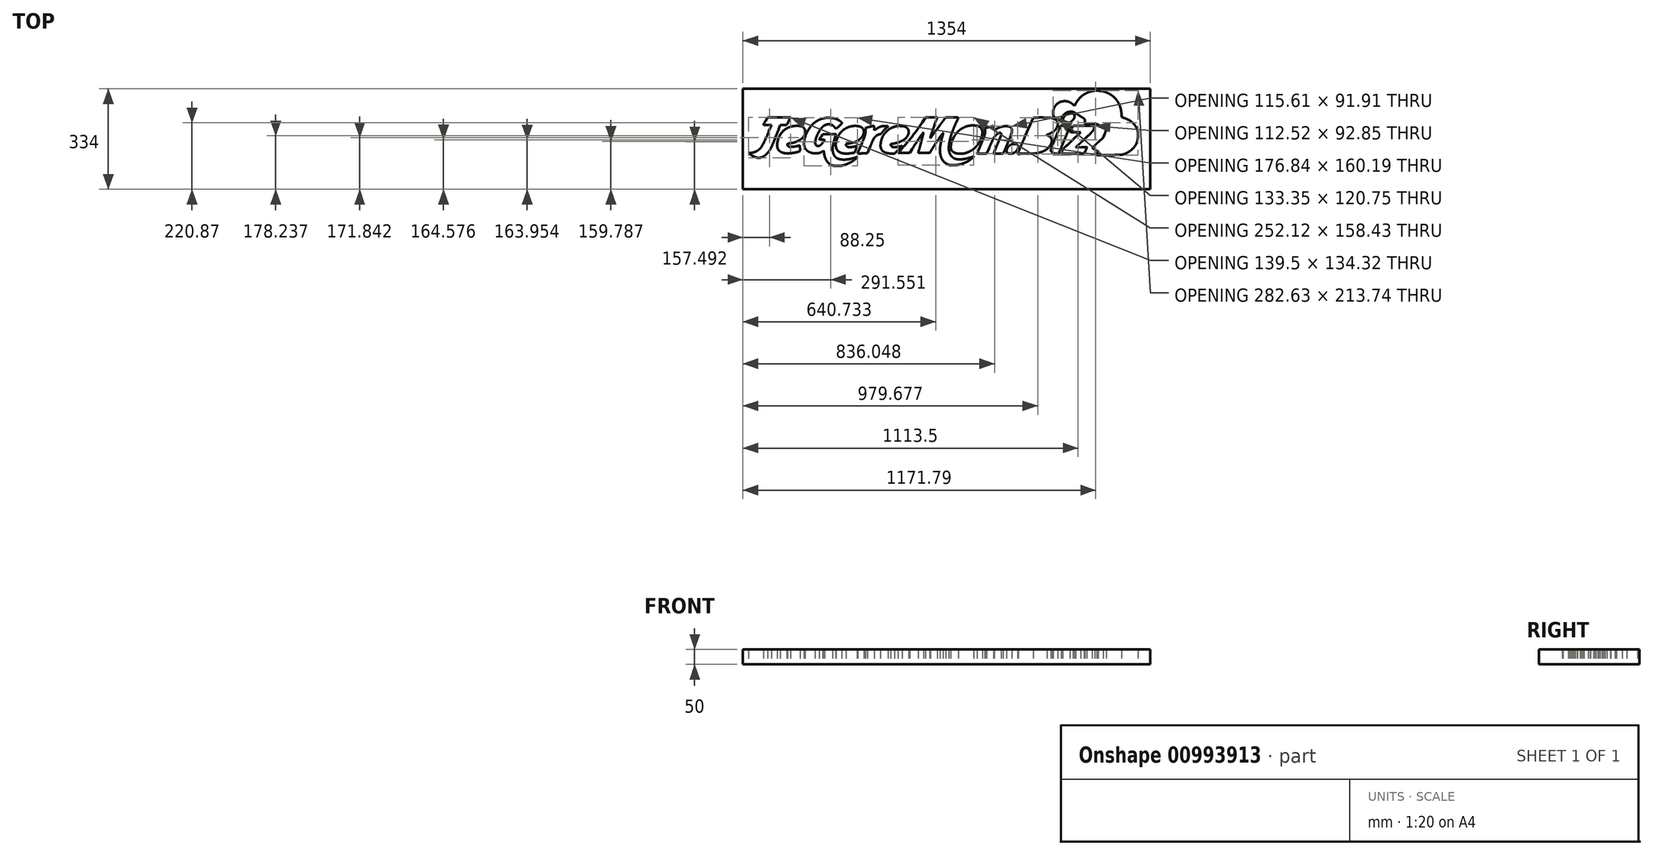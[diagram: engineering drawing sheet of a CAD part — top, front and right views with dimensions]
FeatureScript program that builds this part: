
annotation { "Feature Type Name" : "Feature", "Feature Type Description" : "" }
export const myFeature = defineFeature(function(context is Context, id is Id, definition is map)
    precondition{}
    {
        {
            var Q0;
            Q0=qCreatedBy(makeId("Top.planeOp"),FACE);
            var sketch = newSketch(context, id + "F0", { "sketchPlane" : qUnion([Q0])});
            skLineSegment(sketch, "E0", {"start": v(-677, 0) * mm, "end": v(-677, -167) * mm});
            skLineSegment(sketch, "E1", {"start": v(-677, -167) * mm, "end": v(0, -167) * mm});
            skLineSegment(sketch, "E2", {"start": v(0, -167) * mm, "end": v(677, -167) * mm});
            skLineSegment(sketch, "E3", {"start": v(677, -167) * mm, "end": v(677, 0) * mm});
            skLineSegment(sketch, "E4", {"start": v(677, 0) * mm, "end": v(677, 167) * mm});
            skLineSegment(sketch, "E5", {"start": v(677, 167) * mm, "end": v(0, 167) * mm});
            skLineSegment(sketch, "E6", {"start": v(0, 167) * mm, "end": v(-677, 167) * mm});
            skLineSegment(sketch, "E7", {"start": v(-677, 167) * mm, "end": v(-677, 0) * mm});
            skArc(sketch, "E8", {"start": v(522.85, 158.05) * mm, "mid": v(532, 154.5) * mm, "end": v(540.8, 150.2) * mm});
            skArc(sketch, "E9", {"start": v(540.8, 150.2) * mm, "mid": v(548.3, 145.56) * mm, "end": v(555.24, 140.1) * mm});
            skArc(sketch, "E10", {"start": v(555.24, 140.1) * mm, "mid": v(561.22, 134.1) * mm, "end": v(566.43, 127.43) * mm});
            skArc(sketch, "E11", {"start": v(566.43, 127.43) * mm, "mid": v(571, 119.94) * mm, "end": v(574.75, 112) * mm});
            skArc(sketch, "E12", {"start": v(574.75, 112) * mm, "mid": v(576.07, 108.55) * mm, "end": v(577.26, 105.05) * mm});
            skArc(sketch, "E13", {"start": v(577.26, 105.05) * mm, "mid": v(578.21, 101.76) * mm, "end": v(579, 98.43) * mm});
            skArc(sketch, "E14", {"start": v(579, 98.43) * mm, "mid": v(579.66, 94.87) * mm, "end": v(580.16, 91.29) * mm});
            skArc(sketch, "E15", {"start": v(580.16, 91.29) * mm, "mid": v(580.6, 87) * mm, "end": v(580.91, 82.7) * mm});
            skLineSegment(sketch, "E16", {"start": v(580.91, 82.7) * mm, "end": v(581.5, 72.9) * mm});
            skLineSegment(sketch, "E17", {"start": v(581.5, 72.9) * mm, "end": v(590.5, 69.9) * mm});
            skArc(sketch, "E18", {"start": v(590.5, 69.9) * mm, "mid": v(598.28, 66.89) * mm, "end": v(605.75, 63.2) * mm});
            skArc(sketch, "E19", {"start": v(605.75, 63.2) * mm, "mid": v(612.16, 59.14) * mm, "end": v(618.04, 54.34) * mm});
            skArc(sketch, "E20", {"start": v(618.04, 54.34) * mm, "mid": v(623.04, 49.1) * mm, "end": v(627.33, 43.28) * mm});
            skArc(sketch, "E21", {"start": v(627.33, 43.28) * mm, "mid": v(630.92, 36.86) * mm, "end": v(633.71, 30.06) * mm});
            skArc(sketch, "E22", {"start": v(633.71, 30.06) * mm, "mid": v(635.18, 24.64) * mm, "end": v(635.92, 19.07) * mm});
            skArc(sketch, "E23", {"start": v(635.92, 19.07) * mm, "mid": v(636.1, 12.6) * mm, "end": v(635.72, 6.13) * mm});
            skArc(sketch, "E24", {"start": v(635.72, 6.13) * mm, "mid": v(634.77, -0.46) * mm, "end": v(633.28, -6.94) * mm});
            skArc(sketch, "E25", {"start": v(633.28, -6.94) * mm, "mid": v(631.36, -12.75) * mm, "end": v(628.82, -18.31) * mm});
            skArc(sketch, "E26", {"start": v(628.82, -18.31) * mm, "mid": v(626.67, -21.97) * mm, "end": v(624.15, -25.39) * mm});
            skArc(sketch, "E27", {"start": v(624.15, -25.39) * mm, "mid": v(620.76, -29.27) * mm, "end": v(617.16, -32.96) * mm});
            skArc(sketch, "E28", {"start": v(617.16, -32.96) * mm, "mid": v(613.27, -36.5) * mm, "end": v(609.2, -39.8) * mm});
            skArc(sketch, "E29", {"start": v(609.2, -39.8) * mm, "mid": v(605.45, -42.4) * mm, "end": v(601.5, -44.67) * mm});
            skArc(sketch, "E30", {"start": v(601.5, -44.67) * mm, "mid": v(596.03, -47.31) * mm, "end": v(590.44, -49.66) * mm});
            skArc(sketch, "E31", {"start": v(590.44, -49.66) * mm, "mid": v(586.05, -51.07) * mm, "end": v(581.52, -51.94) * mm});
            skArc(sketch, "E32", {"start": v(581.52, -51.94) * mm, "mid": v(575.4, -52.57) * mm, "end": v(569.24, -52.83) * mm});
            skArc(sketch, "E33", {"start": v(569.24, -52.83) * mm, "mid": v(554.1, -52.96) * mm, "end": v(538.95, -53) * mm});
            skLineSegment(sketch, "E34", {"start": v(538.95, -53) * mm, "end": v(498.1, -53) * mm});
            skLineSegment(sketch, "E35", {"start": v(498.1, -53) * mm, "end": v(499.65, -49.25) * mm});
            skArc(sketch, "E36", {"start": v(499.65, -49.25) * mm, "mid": v(499.98, -48.47) * mm, "end": v(500.34, -47.7) * mm});
            skArc(sketch, "E37", {"start": v(500.34, -47.7) * mm, "mid": v(500.72, -46.93) * mm, "end": v(501.12, -46.16) * mm});
            skArc(sketch, "E38", {"start": v(501.12, -46.16) * mm, "mid": v(501.49, -45.49) * mm, "end": v(501.88, -44.83) * mm});
            skArc(sketch, "E39", {"start": v(501.88, -44.83) * mm, "mid": v(502.16, -44.4) * mm, "end": v(502.47, -44) * mm});
            skArc(sketch, "E40", {"start": v(502.47, -44) * mm, "mid": v(502.91, -43.36) * mm, "end": v(503.22, -42.65) * mm});
            skArc(sketch, "E41", {"start": v(503.22, -42.65) * mm, "mid": v(503.34, -41.99) * mm, "end": v(503.25, -41.32) * mm});
            skArc(sketch, "E42", {"start": v(503.25, -41.32) * mm, "mid": v(503, -40.78) * mm, "end": v(502.56, -40.37) * mm});
            skArc(sketch, "E43", {"start": v(502.56, -40.37) * mm, "mid": v(501.98, -40.1) * mm, "end": v(501.35, -40) * mm});
            skArc(sketch, "E44", {"start": v(501.35, -40) * mm, "mid": v(500.87, -39.95) * mm, "end": v(500.41, -39.78) * mm});
            skArc(sketch, "E45", {"start": v(500.41, -39.78) * mm, "mid": v(499.1, -39.14) * mm, "end": v(497.81, -38.48) * mm});
            skArc(sketch, "E46", {"start": v(497.81, -38.48) * mm, "mid": v(496.27, -37.66) * mm, "end": v(494.75, -36.8) * mm});
            skArc(sketch, "E47", {"start": v(494.75, -36.8) * mm, "mid": v(493.06, -35.82) * mm, "end": v(491.4, -34.82) * mm});
            skLineSegment(sketch, "E48", {"start": v(491.4, -34.82) * mm, "end": v(482.9, -29.64) * mm});
            skLineSegment(sketch, "E49", {"start": v(482.9, -29.64) * mm, "end": v(485.2, -27.5) * mm});
            skArc(sketch, "E50", {"start": v(485.2, -27.5) * mm, "mid": v(485.98, -26.77) * mm, "end": v(486.76, -26.04) * mm});
            skArc(sketch, "E51", {"start": v(486.76, -26.04) * mm, "mid": v(489.16, -23.78) * mm, "end": v(491.56, -21.52) * mm});
            skArc(sketch, "E52", {"start": v(491.56, -21.52) * mm, "mid": v(494.42, -18.83) * mm, "end": v(497.27, -16.14) * mm});
            skArc(sketch, "E53", {"start": v(497.27, -16.14) * mm, "mid": v(500.44, -13.15) * mm, "end": v(503.61, -10.16) * mm});
            skLineSegment(sketch, "E54", {"start": v(503.61, -10.16) * mm, "end": v(519.72, 5.04) * mm});
            skLineSegment(sketch, "E55", {"start": v(519.72, 5.04) * mm, "end": v(525.11, 17.67) * mm});
            skArc(sketch, "E56", {"start": v(525.11, 17.67) * mm, "mid": v(526.15, 20.11) * mm, "end": v(527.2, 22.56) * mm});
            skArc(sketch, "E57", {"start": v(527.2, 22.56) * mm, "mid": v(528.1, 24.68) * mm, "end": v(529, 26.8) * mm});
            skArc(sketch, "E58", {"start": v(529, 26.8) * mm, "mid": v(529.78, 28.64) * mm, "end": v(530.56, 30.47) * mm});
            skArc(sketch, "E59", {"start": v(530.56, 30.47) * mm, "mid": v(530.68, 30.75) * mm, "end": v(530.8, 31.03) * mm});
            skArc(sketch, "E60", {"start": v(530.8, 31.03) * mm, "mid": v(530.81, 31.76) * mm, "end": v(530.36, 32.33) * mm});
            skArc(sketch, "E61", {"start": v(530.36, 32.33) * mm, "mid": v(523.65, 36.39) * mm, "end": v(516.92, 40.42) * mm});
            skArc(sketch, "E62", {"start": v(516.92, 40.42) * mm, "mid": v(510.2, 44.42) * mm, "end": v(503.49, 48.39) * mm});
            skArc(sketch, "E63", {"start": v(503.49, 48.39) * mm, "mid": v(502.63, 48.61) * mm, "end": v(501.79, 48.37) * mm});
            skArc(sketch, "E64", {"start": v(501.79, 48.37) * mm, "mid": v(501.58, 48.25) * mm, "end": v(501.37, 48.15) * mm});
            skArc(sketch, "E65", {"start": v(501.37, 48.15) * mm, "mid": v(501.27, 48.14) * mm, "end": v(501.19, 48.2) * mm});
            skArc(sketch, "E66", {"start": v(501.19, 48.2) * mm, "mid": v(501.15, 48.3) * mm, "end": v(501.16, 48.4) * mm});
            skArc(sketch, "E67", {"start": v(501.16, 48.4) * mm, "mid": v(501.28, 48.63) * mm, "end": v(501.4, 48.85) * mm});
            skArc(sketch, "E68", {"start": v(501.4, 48.85) * mm, "mid": v(501.42, 49.22) * mm, "end": v(501.11, 49.44) * mm});
            skArc(sketch, "E69", {"start": v(501.11, 49.44) * mm, "mid": v(499.1, 49.61) * mm, "end": v(497.1, 49.75) * mm});
            skArc(sketch, "E70", {"start": v(497.1, 49.75) * mm, "mid": v(493.96, 49.88) * mm, "end": v(490.81, 49.95) * mm});
            skArc(sketch, "E71", {"start": v(490.81, 49.95) * mm, "mid": v(485.46, 49.99) * mm, "end": v(480.11, 50) * mm});
            skLineSegment(sketch, "E72", {"start": v(480.11, 50) * mm, "end": v(458.1, 50) * mm});
            skLineSegment(sketch, "E73", {"start": v(458.1, 50) * mm, "end": v(459.17, 53.07) * mm});
            skArc(sketch, "E74", {"start": v(459.17, 53.07) * mm, "mid": v(459.6, 54.6) * mm, "end": v(459.8, 56.18) * mm});
            skArc(sketch, "E75", {"start": v(459.8, 56.18) * mm, "mid": v(459.82, 58.07) * mm, "end": v(459.68, 59.94) * mm});
            skArc(sketch, "E76", {"start": v(459.68, 59.94) * mm, "mid": v(459.39, 61.8) * mm, "end": v(458.94, 63.6) * mm});
            skArc(sketch, "E77", {"start": v(458.94, 63.6) * mm, "mid": v(458.4, 65.06) * mm, "end": v(457.65, 66.42) * mm});
            skArc(sketch, "E78", {"start": v(457.65, 66.42) * mm, "mid": v(456.4, 67.93) * mm, "end": v(454.89, 69.16) * mm});
            skArc(sketch, "E79", {"start": v(454.89, 69.16) * mm, "mid": v(447.55, 73.87) * mm, "end": v(440.2, 78.54) * mm});
            skArc(sketch, "E80", {"start": v(440.2, 78.54) * mm, "mid": v(433.08, 82.98) * mm, "end": v(425.92, 87.36) * mm});
            skArc(sketch, "E81", {"start": v(425.92, 87.36) * mm, "mid": v(423.06, 88.9) * mm, "end": v(420.04, 90.14) * mm});
            skArc(sketch, "E82", {"start": v(420.04, 90.14) * mm, "mid": v(417.9, 90.7) * mm, "end": v(415.7, 90.92) * mm});
            skArc(sketch, "E83", {"start": v(415.7, 90.92) * mm, "mid": v(412.64, 90.9) * mm, "end": v(409.59, 90.7) * mm});
            skArc(sketch, "E84", {"start": v(409.59, 90.7) * mm, "mid": v(406.46, 90.3) * mm, "end": v(403.37, 89.7) * mm});
            skArc(sketch, "E85", {"start": v(403.37, 89.7) * mm, "mid": v(400.93, 89.01) * mm, "end": v(398.59, 88.04) * mm});
            skArc(sketch, "E86", {"start": v(398.59, 88.04) * mm, "mid": v(395.15, 86.1) * mm, "end": v(392, 83.7) * mm});
            skArc(sketch, "E87", {"start": v(392, 83.7) * mm, "mid": v(389, 80.78) * mm, "end": v(386.32, 77.55) * mm});
            skArc(sketch, "E88", {"start": v(386.32, 77.55) * mm, "mid": v(384.13, 74.2) * mm, "end": v(382.33, 70.62) * mm});
            skArc(sketch, "E89", {"start": v(382.33, 70.62) * mm, "mid": v(381.27, 67.38) * mm, "end": v(380.83, 64) * mm});
            skArc(sketch, "E90", {"start": v(380.83, 64) * mm, "mid": v(380.79, 63.23) * mm, "end": v(380.73, 62.46) * mm});
            skArc(sketch, "E91", {"start": v(380.73, 62.46) * mm, "mid": v(380.66, 61.82) * mm, "end": v(380.56, 61.17) * mm});
            skArc(sketch, "E92", {"start": v(380.56, 61.17) * mm, "mid": v(380.46, 60.67) * mm, "end": v(380.35, 60.17) * mm});
            skArc(sketch, "E93", {"start": v(380.35, 60.17) * mm, "mid": v(380.27, 60.05) * mm, "end": v(380.13, 60) * mm});
            skArc(sketch, "E94", {"start": v(380.13, 60) * mm, "mid": v(379.93, 60.03) * mm, "end": v(379.75, 60.1) * mm});
            skArc(sketch, "E95", {"start": v(379.75, 60.1) * mm, "mid": v(378.47, 60.86) * mm, "end": v(377.2, 61.62) * mm});
            skArc(sketch, "E96", {"start": v(377.2, 61.62) * mm, "mid": v(375.73, 62.5) * mm, "end": v(374.27, 63.4) * mm});
            skArc(sketch, "E97", {"start": v(374.27, 63.4) * mm, "mid": v(372.59, 64.44) * mm, "end": v(370.9, 65.5) * mm});
            skArc(sketch, "E98", {"start": v(370.9, 65.5) * mm, "mid": v(369.12, 66.62) * mm, "end": v(367.33, 67.72) * mm});
            skArc(sketch, "E99", {"start": v(367.33, 67.72) * mm, "mid": v(365.54, 68.78) * mm, "end": v(363.74, 69.82) * mm});
            skArc(sketch, "E100", {"start": v(363.74, 69.82) * mm, "mid": v(362.18, 70.7) * mm, "end": v(360.6, 71.57) * mm});
            skArc(sketch, "E101", {"start": v(360.6, 71.57) * mm, "mid": v(359.67, 72.05) * mm, "end": v(358.7, 72.48) * mm});
            skArc(sketch, "E102", {"start": v(358.7, 72.48) * mm, "mid": v(357.65, 72.98) * mm, "end": v(356.64, 73.56) * mm});
            skArc(sketch, "E103", {"start": v(356.64, 73.56) * mm, "mid": v(356, 74.08) * mm, "end": v(355.53, 74.73) * mm});
            skArc(sketch, "E104", {"start": v(355.53, 74.73) * mm, "mid": v(355.1, 75.65) * mm, "end": v(354.82, 76.62) * mm});
            skArc(sketch, "E105", {"start": v(354.82, 76.62) * mm, "mid": v(354.4, 78.74) * mm, "end": v(354.02, 80.86) * mm});
            skArc(sketch, "E106", {"start": v(354.02, 80.86) * mm, "mid": v(353.52, 85.47) * mm, "end": v(353.57, 90.11) * mm});
            skArc(sketch, "E107", {"start": v(353.57, 90.11) * mm, "mid": v(354.16, 94.7) * mm, "end": v(355.29, 99.2) * mm});
            skArc(sketch, "E108", {"start": v(355.29, 99.2) * mm, "mid": v(356.93, 103.51) * mm, "end": v(359.07, 107.6) * mm});
            skArc(sketch, "E109", {"start": v(359.07, 107.6) * mm, "mid": v(361.67, 111.37) * mm, "end": v(364.7, 114.8) * mm});
            skArc(sketch, "E110", {"start": v(364.7, 114.8) * mm, "mid": v(370.61, 119.65) * mm, "end": v(377.35, 123.25) * mm});
            skArc(sketch, "E111", {"start": v(377.35, 123.25) * mm, "mid": v(384.7, 125.47) * mm, "end": v(392.32, 126.24) * mm});
            skArc(sketch, "E112", {"start": v(392.32, 126.24) * mm, "mid": v(399.91, 125.5) * mm, "end": v(407.21, 123.3) * mm});
            skArc(sketch, "E113", {"start": v(407.21, 123.3) * mm, "mid": v(413.87, 119.74) * mm, "end": v(419.68, 114.92) * mm});
            skLineSegment(sketch, "E114", {"start": v(419.68, 114.92) * mm, "end": v(424.35, 110.16) * mm});
            skLineSegment(sketch, "E115", {"start": v(424.35, 110.16) * mm, "end": v(428.65, 117.7) * mm});
            skArc(sketch, "E116", {"start": v(428.65, 117.7) * mm, "mid": v(433.74, 125.78) * mm, "end": v(439.52, 133.38) * mm});
            skArc(sketch, "E117", {"start": v(439.52, 133.38) * mm, "mid": v(445.5, 139.78) * mm, "end": v(452.18, 145.46) * mm});
            skArc(sketch, "E118", {"start": v(452.18, 145.46) * mm, "mid": v(459.3, 150.21) * mm, "end": v(466.93, 154.1) * mm});
            skArc(sketch, "E119", {"start": v(466.93, 154.1) * mm, "mid": v(475.33, 157.27) * mm, "end": v(484, 159.57) * mm});
            skArc(sketch, "E120", {"start": v(484, 159.57) * mm, "mid": v(488.3, 160.28) * mm, "end": v(492.64, 160.63) * mm});
            skArc(sketch, "E121", {"start": v(492.64, 160.63) * mm, "mid": v(498.35, 160.74) * mm, "end": v(504.06, 160.63) * mm});
            skArc(sketch, "E122", {"start": v(504.06, 160.63) * mm, "mid": v(509.66, 160.3) * mm, "end": v(515.23, 159.77) * mm});
            skArc(sketch, "E123", {"start": v(515.23, 159.77) * mm, "mid": v(519.09, 159.11) * mm, "end": v(522.85, 158.05) * mm});
            skArc(sketch, "E124", {"start": v(419.45, 84.58) * mm, "mid": v(421.84, 83.12) * mm, "end": v(423.67, 81) * mm});
            skArc(sketch, "E125", {"start": v(423.67, 81) * mm, "mid": v(424.78, 78.4) * mm, "end": v(425.08, 75.6) * mm});
            skArc(sketch, "E126", {"start": v(425.08, 75.6) * mm, "mid": v(424.54, 72.17) * mm, "end": v(423.26, 68.95) * mm});
            skArc(sketch, "E127", {"start": v(423.26, 68.95) * mm, "mid": v(421.05, 65.34) * mm, "end": v(418.42, 62.04) * mm});
            skArc(sketch, "E128", {"start": v(418.42, 62.04) * mm, "mid": v(416.33, 59.9) * mm, "end": v(414.08, 57.94) * mm});
            skArc(sketch, "E129", {"start": v(414.08, 57.94) * mm, "mid": v(412.04, 56.51) * mm, "end": v(409.82, 55.37) * mm});
            skArc(sketch, "E130", {"start": v(409.82, 55.37) * mm, "mid": v(407.43, 54.53) * mm, "end": v(404.95, 54) * mm});
            skArc(sketch, "E131", {"start": v(404.95, 54) * mm, "mid": v(401.81, 53.66) * mm, "end": v(398.67, 53.53) * mm});
            skArc(sketch, "E132", {"start": v(398.67, 53.53) * mm, "mid": v(396.27, 53.54) * mm, "end": v(393.88, 53.59) * mm});
            skArc(sketch, "E133", {"start": v(393.88, 53.59) * mm, "mid": v(392.74, 53.69) * mm, "end": v(391.63, 53.92) * mm});
            skArc(sketch, "E134", {"start": v(391.63, 53.92) * mm, "mid": v(390.81, 54.23) * mm, "end": v(390.07, 54.7) * mm});
            skArc(sketch, "E135", {"start": v(390.07, 54.7) * mm, "mid": v(389.2, 55.47) * mm, "end": v(388.42, 56.3) * mm});
            skArc(sketch, "E136", {"start": v(388.42, 56.3) * mm, "mid": v(387.41, 57.7) * mm, "end": v(386.67, 59.26) * mm});
            skArc(sketch, "E137", {"start": v(386.67, 59.26) * mm, "mid": v(386.22, 60.92) * mm, "end": v(386.07, 62.64) * mm});
            skArc(sketch, "E138", {"start": v(386.07, 62.64) * mm, "mid": v(386.22, 64.6) * mm, "end": v(386.67, 66.5) * mm});
            skArc(sketch, "E139", {"start": v(386.67, 66.5) * mm, "mid": v(387.47, 68.75) * mm, "end": v(388.46, 70.92) * mm});
            skArc(sketch, "E140", {"start": v(388.46, 70.92) * mm, "mid": v(390.96, 74.92) * mm, "end": v(394.13, 78.4) * mm});
            skArc(sketch, "E141", {"start": v(394.13, 78.4) * mm, "mid": v(397.97, 81.39) * mm, "end": v(402.24, 83.7) * mm});
            skArc(sketch, "E142", {"start": v(402.24, 83.7) * mm, "mid": v(406.64, 85.2) * mm, "end": v(411.23, 85.93) * mm});
            skArc(sketch, "E143", {"start": v(411.23, 85.93) * mm, "mid": v(415.42, 85.74) * mm, "end": v(419.45, 84.58) * mm});
            skArc(sketch, "E144", {"start": v(-519, 71.48) * mm, "mid": v(-519.02, 71.29) * mm, "end": v(-519.09, 71.1) * mm});
            skArc(sketch, "E145", {"start": v(-519.09, 71.1) * mm, "mid": v(-519.92, 69.35) * mm, "end": v(-520.76, 67.6) * mm});
            skArc(sketch, "E146", {"start": v(-520.76, 67.6) * mm, "mid": v(-521.73, 65.6) * mm, "end": v(-522.7, 63.62) * mm});
            skArc(sketch, "E147", {"start": v(-522.7, 63.62) * mm, "mid": v(-523.85, 61.3) * mm, "end": v(-525, 58.98) * mm});
            skLineSegment(sketch, "E148", {"start": v(-525, 58.98) * mm, "end": v(-531.02, 47) * mm});
            skLineSegment(sketch, "E149", {"start": v(-531.02, 47) * mm, "end": v(-541.9, 47) * mm});
            skLineSegment(sketch, "E150", {"start": v(-541.9, 47) * mm, "end": v(-552.77, 47) * mm});
            skLineSegment(sketch, "E151", {"start": v(-552.77, 47) * mm, "end": v(-557.52, 34.75) * mm});
            skArc(sketch, "E152", {"start": v(-557.52, 34.75) * mm, "mid": v(-565.77, 13.62) * mm, "end": v(-574.1, -7.48) * mm});
            skArc(sketch, "E153", {"start": v(-574.1, -7.48) * mm, "mid": v(-578.13, -17.16) * mm, "end": v(-582.48, -26.69) * mm});
            skArc(sketch, "E154", {"start": v(-582.48, -26.69) * mm, "mid": v(-585.63, -32.74) * mm, "end": v(-589.2, -38.56) * mm});
            skArc(sketch, "E155", {"start": v(-589.2, -38.56) * mm, "mid": v(-592.98, -43.73) * mm, "end": v(-597.2, -48.56) * mm});
            skArc(sketch, "E156", {"start": v(-597.2, -48.56) * mm, "mid": v(-600.98, -52.22) * mm, "end": v(-605.07, -55.53) * mm});
            skArc(sketch, "E157", {"start": v(-605.07, -55.53) * mm, "mid": v(-609, -58.05) * mm, "end": v(-613.2, -60.07) * mm});
            skArc(sketch, "E158", {"start": v(-613.2, -60.07) * mm, "mid": v(-617.28, -61.4) * mm, "end": v(-621.52, -62.15) * mm});
            skArc(sketch, "E159", {"start": v(-621.52, -62.15) * mm, "mid": v(-625.77, -62.3) * mm, "end": v(-630, -61.83) * mm});
            skArc(sketch, "E160", {"start": v(-630, -61.83) * mm, "mid": v(-632.8, -61.17) * mm, "end": v(-635.52, -60.24) * mm});
            skArc(sketch, "E161", {"start": v(-635.52, -60.24) * mm, "mid": v(-639.06, -58.73) * mm, "end": v(-642.54, -57.08) * mm});
            skArc(sketch, "E162", {"start": v(-642.54, -57.08) * mm, "mid": v(-646.01, -55.24) * mm, "end": v(-649.4, -53.26) * mm});
            skArc(sketch, "E163", {"start": v(-649.4, -53.26) * mm, "mid": v(-652.03, -51.5) * mm, "end": v(-654.5, -49.53) * mm});
            skLineSegment(sketch, "E164", {"start": v(-654.5, -49.53) * mm, "end": v(-658.5, -46.08) * mm});
            skLineSegment(sketch, "E165", {"start": v(-658.5, -46.08) * mm, "end": v(-653.8, -46.04) * mm});
            skArc(sketch, "E166", {"start": v(-653.8, -46.04) * mm, "mid": v(-649.06, -45.75) * mm, "end": v(-644.38, -44.96) * mm});
            skArc(sketch, "E167", {"start": v(-644.38, -44.96) * mm, "mid": v(-639.7, -43.67) * mm, "end": v(-635.16, -41.92) * mm});
            skArc(sketch, "E168", {"start": v(-635.16, -41.92) * mm, "mid": v(-630.81, -39.74) * mm, "end": v(-626.7, -37.14) * mm});
            skArc(sketch, "E169", {"start": v(-626.7, -37.14) * mm, "mid": v(-622.96, -34.2) * mm, "end": v(-619.55, -30.88) * mm});
            skArc(sketch, "E170", {"start": v(-619.55, -30.88) * mm, "mid": v(-616.6, -27.33) * mm, "end": v(-614.05, -23.5) * mm});
            skArc(sketch, "E171", {"start": v(-614.05, -23.5) * mm, "mid": v(-610.53, -17.32) * mm, "end": v(-607.2, -11.04) * mm});
            skArc(sketch, "E172", {"start": v(-607.2, -11.04) * mm, "mid": v(-603.17, -2.88) * mm, "end": v(-599.36, 5.4) * mm});
            skArc(sketch, "E173", {"start": v(-599.36, 5.4) * mm, "mid": v(-594.88, 15.67) * mm, "end": v(-590.54, 26) * mm});
            skLineSegment(sketch, "E174", {"start": v(-590.54, 26) * mm, "end": v(-582.12, 46.5) * mm});
            skLineSegment(sketch, "E175", {"start": v(-582.12, 46.5) * mm, "end": v(-595.65, 46.78) * mm});
            skArc(sketch, "E176", {"start": v(-595.65, 46.78) * mm, "mid": v(-599.58, 46.87) * mm, "end": v(-603.5, 46.99) * mm});
            skArc(sketch, "E177", {"start": v(-603.5, 46.99) * mm, "mid": v(-605.17, 47.09) * mm, "end": v(-606.82, 47.28) * mm});
            skArc(sketch, "E178", {"start": v(-606.82, 47.28) * mm, "mid": v(-607.57, 47.47) * mm, "end": v(-608.27, 47.8) * mm});
            skArc(sketch, "E179", {"start": v(-608.27, 47.8) * mm, "mid": v(-608.58, 48.19) * mm, "end": v(-608.57, 48.68) * mm});
            skArc(sketch, "E180", {"start": v(-608.57, 48.68) * mm, "mid": v(-608.34, 49.22) * mm, "end": v(-608.07, 49.74) * mm});
            skArc(sketch, "E181", {"start": v(-608.07, 49.74) * mm, "mid": v(-607.14, 51.38) * mm, "end": v(-606.21, 53) * mm});
            skArc(sketch, "E182", {"start": v(-606.21, 53) * mm, "mid": v(-605.1, 54.94) * mm, "end": v(-603.96, 56.87) * mm});
            skArc(sketch, "E183", {"start": v(-603.96, 56.87) * mm, "mid": v(-602.7, 59.01) * mm, "end": v(-601.41, 61.15) * mm});
            skLineSegment(sketch, "E184", {"start": v(-601.41, 61.15) * mm, "end": v(-594.87, 72) * mm});
            skLineSegment(sketch, "E185", {"start": v(-594.87, 72) * mm, "end": v(-556.94, 72) * mm});
            skArc(sketch, "E186", {"start": v(-556.94, 72) * mm, "mid": v(-549.66, 72) * mm, "end": v(-542.39, 71.96) * mm});
            skArc(sketch, "E187", {"start": v(-542.39, 71.96) * mm, "mid": v(-536.27, 71.92) * mm, "end": v(-530.14, 71.85) * mm});
            skArc(sketch, "E188", {"start": v(-530.14, 71.85) * mm, "mid": v(-524.68, 71.77) * mm, "end": v(-519.2, 71.7) * mm});
            skArc(sketch, "E189", {"start": v(-519.2, 71.7) * mm, "mid": v(-519.06, 71.63) * mm, "end": v(-519, 71.48) * mm});
            skArc(sketch, "E190", {"start": v(-31, 71.58) * mm, "mid": v(-31.01, 71.43) * mm, "end": v(-31.05, 71.29) * mm});
            skArc(sketch, "E191", {"start": v(-31.05, 71.29) * mm, "mid": v(-31.32, 70.6) * mm, "end": v(-31.58, 69.93) * mm});
            skArc(sketch, "E192", {"start": v(-31.58, 69.93) * mm, "mid": v(-31.9, 69.13) * mm, "end": v(-32.23, 68.33) * mm});
            skArc(sketch, "E193", {"start": v(-32.23, 68.33) * mm, "mid": v(-32.6, 67.43) * mm, "end": v(-32.99, 66.53) * mm});
            skArc(sketch, "E194", {"start": v(-32.99, 66.53) * mm, "mid": v(-35.76, 59.78) * mm, "end": v(-38.32, 52.94) * mm});
            skArc(sketch, "E195", {"start": v(-38.32, 52.94) * mm, "mid": v(-42.08, 42.26) * mm, "end": v(-45.75, 31.53) * mm});
            skArc(sketch, "E196", {"start": v(-45.75, 31.53) * mm, "mid": v(-49.5, 20.33) * mm, "end": v(-53.21, 9.12) * mm});
            skArc(sketch, "E197", {"start": v(-53.21, 9.12) * mm, "mid": v(-53.8, 6.69) * mm, "end": v(-54, 4.2) * mm});
            skArc(sketch, "E198", {"start": v(-54, 4.2) * mm, "mid": v(-53.88, 4.03) * mm, "end": v(-53.68, 4.1) * mm});
            skArc(sketch, "E199", {"start": v(-53.68, 4.1) * mm, "mid": v(-44.83, 15.92) * mm, "end": v(-35.99, 27.74) * mm});
            skArc(sketch, "E200", {"start": v(-35.99, 27.74) * mm, "mid": v(-28.12, 38.3) * mm, "end": v(-20.28, 48.87) * mm});
            skArc(sketch, "E201", {"start": v(-20.28, 48.87) * mm, "mid": v(-15.4, 55.54) * mm, "end": v(-10.6, 62.25) * mm});
            skLineSegment(sketch, "E202", {"start": v(-10.6, 62.25) * mm, "end": v(-3.69, 72) * mm});
            skLineSegment(sketch, "E203", {"start": v(-3.69, 72) * mm, "end": v(17.66, 72) * mm});
            skArc(sketch, "E204", {"start": v(17.66, 72) * mm, "mid": v(21.75, 71.98) * mm, "end": v(25.84, 71.94) * mm});
            skArc(sketch, "E205", {"start": v(25.84, 71.94) * mm, "mid": v(29.29, 71.86) * mm, "end": v(32.73, 71.74) * mm});
            skArc(sketch, "E206", {"start": v(32.73, 71.74) * mm, "mid": v(35.7, 71.62) * mm, "end": v(38.66, 71.48) * mm});
            skArc(sketch, "E207", {"start": v(38.66, 71.48) * mm, "mid": v(38.9, 71.37) * mm, "end": v(39, 71.13) * mm});
            skArc(sketch, "E208", {"start": v(39, 71.13) * mm, "mid": v(38.96, 70.8) * mm, "end": v(38.86, 70.49) * mm});
            skArc(sketch, "E209", {"start": v(38.86, 70.49) * mm, "mid": v(37.77, 68.1) * mm, "end": v(36.67, 65.7) * mm});
            skArc(sketch, "E210", {"start": v(36.67, 65.7) * mm, "mid": v(35.4, 62.96) * mm, "end": v(34.1, 60.22) * mm});
            skArc(sketch, "E211", {"start": v(34.1, 60.22) * mm, "mid": v(32.6, 57.05) * mm, "end": v(31.07, 53.88) * mm});
            skArc(sketch, "E212", {"start": v(31.07, 53.88) * mm, "mid": v(27.36, 45.88) * mm, "end": v(23.92, 37.77) * mm});
            skArc(sketch, "E213", {"start": v(23.92, 37.77) * mm, "mid": v(20.52, 29) * mm, "end": v(17.36, 20.15) * mm});
            skArc(sketch, "E214", {"start": v(17.36, 20.15) * mm, "mid": v(14.6, 11.66) * mm, "end": v(12.08, 3.1) * mm});
            skArc(sketch, "E215", {"start": v(12.08, 3.1) * mm, "mid": v(10.3, -3.98) * mm, "end": v(8.88, -11.13) * mm});
            skArc(sketch, "E216", {"start": v(8.88, -11.13) * mm, "mid": v(7.77, -19.03) * mm, "end": v(7.15, -26.98) * mm});
            skArc(sketch, "E217", {"start": v(7.15, -26.98) * mm, "mid": v(7.2, -33.42) * mm, "end": v(8, -39.8) * mm});
            skArc(sketch, "E218", {"start": v(8, -39.8) * mm, "mid": v(9.35, -45.12) * mm, "end": v(11.44, -50.2) * mm});
            skArc(sketch, "E219", {"start": v(11.44, -50.2) * mm, "mid": v(14.14, -54.67) * mm, "end": v(17.52, -58.65) * mm});
            skArc(sketch, "E220", {"start": v(17.52, -58.65) * mm, "mid": v(20.06, -60.94) * mm, "end": v(22.82, -62.97) * mm});
            skArc(sketch, "E221", {"start": v(22.82, -62.97) * mm, "mid": v(25.5, -64.48) * mm, "end": v(28.38, -65.61) * mm});
            skArc(sketch, "E222", {"start": v(28.38, -65.61) * mm, "mid": v(31.8, -66.49) * mm, "end": v(35.3, -66.98) * mm});
            skArc(sketch, "E223", {"start": v(35.3, -66.98) * mm, "mid": v(40.15, -67.27) * mm, "end": v(45, -67.35) * mm});
            skArc(sketch, "E224", {"start": v(45, -67.35) * mm, "mid": v(49.23, -67.23) * mm, "end": v(53.46, -66.93) * mm});
            skArc(sketch, "E225", {"start": v(53.46, -66.93) * mm, "mid": v(57.6, -66.47) * mm, "end": v(61.72, -65.82) * mm});
            skArc(sketch, "E226", {"start": v(61.72, -65.82) * mm, "mid": v(66.12, -64.93) * mm, "end": v(70.48, -63.87) * mm});
            skArc(sketch, "E227", {"start": v(70.48, -63.87) * mm, "mid": v(75.49, -62.48) * mm, "end": v(80.46, -60.95) * mm});
            skArc(sketch, "E228", {"start": v(80.46, -60.95) * mm, "mid": v(82.18, -60.4) * mm, "end": v(83.91, -59.87) * mm});
            skArc(sketch, "E229", {"start": v(83.91, -59.87) * mm, "mid": v(85.4, -59.44) * mm, "end": v(86.88, -59.02) * mm});
            skArc(sketch, "E230", {"start": v(86.88, -59.02) * mm, "mid": v(88.16, -58.67) * mm, "end": v(89.44, -58.33) * mm});
            skArc(sketch, "E231", {"start": v(89.44, -58.33) * mm, "mid": v(89.6, -58.33) * mm, "end": v(89.74, -58.4) * mm});
            skArc(sketch, "E232", {"start": v(89.74, -58.4) * mm, "mid": v(89.8, -58.53) * mm, "end": v(89.74, -58.66) * mm});
            skArc(sketch, "E233", {"start": v(89.74, -58.66) * mm, "mid": v(89.04, -59.4) * mm, "end": v(88.32, -60.15) * mm});
            skArc(sketch, "E234", {"start": v(88.32, -60.15) * mm, "mid": v(87.46, -61.02) * mm, "end": v(86.58, -61.88) * mm});
            skArc(sketch, "E235", {"start": v(86.58, -61.88) * mm, "mid": v(85.52, -62.88) * mm, "end": v(84.45, -63.88) * mm});
            skArc(sketch, "E236", {"start": v(84.45, -63.88) * mm, "mid": v(80.6, -67.13) * mm, "end": v(76.51, -70.09) * mm});
            skArc(sketch, "E237", {"start": v(76.51, -70.09) * mm, "mid": v(71.88, -72.98) * mm, "end": v(67.07, -75.59) * mm});
            skArc(sketch, "E238", {"start": v(67.07, -75.59) * mm, "mid": v(61.73, -78.1) * mm, "end": v(56.26, -80.32) * mm});
            skArc(sketch, "E239", {"start": v(56.26, -80.32) * mm, "mid": v(50.27, -82.4) * mm, "end": v(44.19, -84.22) * mm});
            skArc(sketch, "E240", {"start": v(44.19, -84.22) * mm, "mid": v(41.95, -84.79) * mm, "end": v(39.68, -85.26) * mm});
            skArc(sketch, "E241", {"start": v(39.68, -85.26) * mm, "mid": v(37.45, -85.64) * mm, "end": v(35.2, -85.91) * mm});
            skArc(sketch, "E242", {"start": v(35.2, -85.91) * mm, "mid": v(32.52, -86.14) * mm, "end": v(29.84, -86.27) * mm});
            skArc(sketch, "E243", {"start": v(29.84, -86.27) * mm, "mid": v(26.17, -86.37) * mm, "end": v(22.5, -86.42) * mm});
            skArc(sketch, "E244", {"start": v(22.5, -86.42) * mm, "mid": v(18.02, -86.42) * mm, "end": v(13.54, -86.4) * mm});
            skArc(sketch, "E245", {"start": v(13.54, -86.4) * mm, "mid": v(11.5, -86.3) * mm, "end": v(9.46, -86.07) * mm});
            skArc(sketch, "E246", {"start": v(9.46, -86.07) * mm, "mid": v(7.82, -85.73) * mm, "end": v(6.22, -85.22) * mm});
            skArc(sketch, "E247", {"start": v(6.22, -85.22) * mm, "mid": v(4, -84.31) * mm, "end": v(1.8, -83.33) * mm});
            skArc(sketch, "E248", {"start": v(1.8, -83.33) * mm, "mid": v(-6.49, -77.94) * mm, "end": v(-13.06, -70.56) * mm});
            skArc(sketch, "E249", {"start": v(-13.06, -70.56) * mm, "mid": v(-18.07, -61.12) * mm, "end": v(-20.99, -50.83) * mm});
            skArc(sketch, "E250", {"start": v(-20.99, -50.83) * mm, "mid": v(-22.23, -37.45) * mm, "end": v(-21.4, -24.04) * mm});
            skArc(sketch, "E251", {"start": v(-21.4, -24.04) * mm, "mid": v(-18.38, -7.14) * mm, "end": v(-14.1, 9.48) * mm});
            skArc(sketch, "E252", {"start": v(-14.1, 9.48) * mm, "mid": v(-13.54, 11.4) * mm, "end": v(-13, 13.33) * mm});
            skArc(sketch, "E253", {"start": v(-13, 13.33) * mm, "mid": v(-12.54, 14.98) * mm, "end": v(-12.1, 16.63) * mm});
            skArc(sketch, "E254", {"start": v(-12.1, 16.63) * mm, "mid": v(-11.73, 18.06) * mm, "end": v(-11.37, 19.5) * mm});
            skArc(sketch, "E255", {"start": v(-11.37, 19.5) * mm, "mid": v(-11.37, 19.65) * mm, "end": v(-11.45, 19.78) * mm});
            skArc(sketch, "E256", {"start": v(-11.45, 19.78) * mm, "mid": v(-12.19, 20.05) * mm, "end": v(-12.87, 19.65) * mm});
            skArc(sketch, "E257", {"start": v(-12.87, 19.65) * mm, "mid": v(-20.68, 8.42) * mm, "end": v(-28.46, -2.83) * mm});
            skArc(sketch, "E258", {"start": v(-28.46, -2.83) * mm, "mid": v(-35.58, -13.25) * mm, "end": v(-42.6, -23.75) * mm});
            skArc(sketch, "E259", {"start": v(-42.6, -23.75) * mm, "mid": v(-47.35, -31.18) * mm, "end": v(-51.89, -38.75) * mm});
            skLineSegment(sketch, "E260", {"start": v(-51.89, -38.75) * mm, "end": v(-56.09, -46) * mm});
            skLineSegment(sketch, "E261", {"start": v(-56.09, -46) * mm, "end": v(-75.04, -46) * mm});
            skArc(sketch, "E262", {"start": v(-75.04, -46) * mm, "mid": v(-78.68, -46) * mm, "end": v(-82.31, -45.98) * mm});
            skArc(sketch, "E263", {"start": v(-82.31, -45.98) * mm, "mid": v(-85.37, -45.96) * mm, "end": v(-88.43, -45.93) * mm});
            skArc(sketch, "E264", {"start": v(-88.43, -45.93) * mm, "mid": v(-91.16, -45.89) * mm, "end": v(-93.9, -45.85) * mm});
            skArc(sketch, "E265", {"start": v(-93.9, -45.85) * mm, "mid": v(-93.97, -45.82) * mm, "end": v(-94, -45.75) * mm});
            skArc(sketch, "E266", {"start": v(-94, -45.75) * mm, "mid": v(-93.98, -45.65) * mm, "end": v(-93.96, -45.55) * mm});
            skArc(sketch, "E267", {"start": v(-93.96, -45.55) * mm, "mid": v(-92.74, -40.72) * mm, "end": v(-91.51, -35.89) * mm});
            skArc(sketch, "E268", {"start": v(-91.51, -35.89) * mm, "mid": v(-90.15, -30.54) * mm, "end": v(-88.79, -25.19) * mm});
            skArc(sketch, "E269", {"start": v(-88.79, -25.19) * mm, "mid": v(-87.17, -18.85) * mm, "end": v(-85.55, -12.52) * mm});
            skArc(sketch, "E270", {"start": v(-85.55, -12.52) * mm, "mid": v(-83.94, -6.2) * mm, "end": v(-82.34, 0.14) * mm});
            skArc(sketch, "E271", {"start": v(-82.34, 0.14) * mm, "mid": v(-81, 5.49) * mm, "end": v(-79.67, 10.84) * mm});
            skArc(sketch, "E272", {"start": v(-79.67, 10.84) * mm, "mid": v(-78.5, 15.65) * mm, "end": v(-77.31, 20.46) * mm});
            skArc(sketch, "E273", {"start": v(-77.31, 20.46) * mm, "mid": v(-77.32, 20.6) * mm, "end": v(-77.38, 20.72) * mm});
            skArc(sketch, "E274", {"start": v(-77.38, 20.72) * mm, "mid": v(-78.08, 20.97) * mm, "end": v(-78.72, 20.6) * mm});
            skArc(sketch, "E275", {"start": v(-78.72, 20.6) * mm, "mid": v(-85.64, 10.6) * mm, "end": v(-92.55, 0.59) * mm});
            skArc(sketch, "E276", {"start": v(-92.55, 0.59) * mm, "mid": v(-99.03, -8.93) * mm, "end": v(-105.4, -18.53) * mm});
            skArc(sketch, "E277", {"start": v(-105.4, -18.53) * mm, "mid": v(-110.24, -26.08) * mm, "end": v(-114.9, -33.75) * mm});
            skLineSegment(sketch, "E278", {"start": v(-114.9, -33.75) * mm, "end": v(-122.14, -46) * mm});
            skLineSegment(sketch, "E279", {"start": v(-122.14, -46) * mm, "end": v(-142.23, -46) * mm});
            skLineSegment(sketch, "E280", {"start": v(-142.23, -46) * mm, "end": v(-162.33, -46) * mm});
            skLineSegment(sketch, "E281", {"start": v(-162.33, -46) * mm, "end": v(-155.9, -39.25) * mm});
            skArc(sketch, "E282", {"start": v(-155.9, -39.25) * mm, "mid": v(-145.97, -28.55) * mm, "end": v(-136.32, -17.6) * mm});
            skArc(sketch, "E283", {"start": v(-136.32, -17.6) * mm, "mid": v(-126.28, -5.67) * mm, "end": v(-116.5, 6.47) * mm});
            skArc(sketch, "E284", {"start": v(-116.5, 6.47) * mm, "mid": v(-106.95, 18.85) * mm, "end": v(-97.66, 31.42) * mm});
            skArc(sketch, "E285", {"start": v(-97.66, 31.42) * mm, "mid": v(-89.18, 43.47) * mm, "end": v(-81, 55.73) * mm});
            skLineSegment(sketch, "E286", {"start": v(-81, 55.73) * mm, "end": v(-70.5, 71.9) * mm});
            skLineSegment(sketch, "E287", {"start": v(-70.5, 71.9) * mm, "end": v(-50.75, 71.95) * mm});
            skArc(sketch, "E288", {"start": v(-50.75, 71.95) * mm, "mid": v(-46.96, 71.95) * mm, "end": v(-43.18, 71.94) * mm});
            skArc(sketch, "E289", {"start": v(-43.18, 71.94) * mm, "mid": v(-39.99, 71.91) * mm, "end": v(-36.8, 71.86) * mm});
            skArc(sketch, "E290", {"start": v(-36.8, 71.86) * mm, "mid": v(-33.98, 71.8) * mm, "end": v(-31.17, 71.75) * mm});
            skArc(sketch, "E291", {"start": v(-31.17, 71.75) * mm, "mid": v(-31.05, 71.7) * mm, "end": v(-31, 71.58) * mm});
            skArc(sketch, "E292", {"start": v(350.5, 69.5) * mm, "mid": v(354.8, 68.14) * mm, "end": v(358.95, 66.39) * mm});
            skArc(sketch, "E293", {"start": v(358.95, 66.39) * mm, "mid": v(362.07, 64.55) * mm, "end": v(364.82, 62.2) * mm});
            skArc(sketch, "E294", {"start": v(364.82, 62.2) * mm, "mid": v(366.8, 59.7) * mm, "end": v(368.23, 56.83) * mm});
            skArc(sketch, "E295", {"start": v(368.23, 56.83) * mm, "mid": v(369.1, 53.61) * mm, "end": v(369.35, 50.29) * mm});
            skArc(sketch, "E296", {"start": v(369.35, 50.29) * mm, "mid": v(369.11, 47.39) * mm, "end": v(368.49, 44.55) * mm});
            skArc(sketch, "E297", {"start": v(368.49, 44.55) * mm, "mid": v(367.4, 41.4) * mm, "end": v(366.04, 38.39) * mm});
            skArc(sketch, "E298", {"start": v(366.04, 38.39) * mm, "mid": v(364.33, 35.36) * mm, "end": v(362.37, 32.49) * mm});
            skArc(sketch, "E299", {"start": v(362.37, 32.49) * mm, "mid": v(360.2, 29.9) * mm, "end": v(357.8, 27.51) * mm});
            skArc(sketch, "E300", {"start": v(357.8, 27.51) * mm, "mid": v(355.46, 25.58) * mm, "end": v(352.95, 23.85) * mm});
            skArc(sketch, "E301", {"start": v(352.95, 23.85) * mm, "mid": v(349.31, 21.65) * mm, "end": v(345.6, 19.56) * mm});
            skArc(sketch, "E302", {"start": v(345.6, 19.56) * mm, "mid": v(341.93, 17.64) * mm, "end": v(338.21, 15.8) * mm});
            skArc(sketch, "E303", {"start": v(338.21, 15.8) * mm, "mid": v(336.5, 15.2) * mm, "end": v(334.68, 15) * mm});
            skArc(sketch, "E304", {"start": v(334.68, 15) * mm, "mid": v(334.02, 14.9) * mm, "end": v(333.42, 14.64) * mm});
            skArc(sketch, "E305", {"start": v(333.42, 14.64) * mm, "mid": v(333.18, 14.28) * mm, "end": v(333.3, 13.88) * mm});
            skArc(sketch, "E306", {"start": v(333.3, 13.88) * mm, "mid": v(334, 13.18) * mm, "end": v(334.83, 12.62) * mm});
            skArc(sketch, "E307", {"start": v(334.83, 12.62) * mm, "mid": v(336.45, 11.76) * mm, "end": v(338.1, 10.96) * mm});
            skArc(sketch, "E308", {"start": v(338.1, 10.96) * mm, "mid": v(341.94, 8.7) * mm, "end": v(345.3, 5.77) * mm});
            skArc(sketch, "E309", {"start": v(345.3, 5.77) * mm, "mid": v(347.62, 2.56) * mm, "end": v(349.03, -1.14) * mm});
            skArc(sketch, "E310", {"start": v(349.03, -1.14) * mm, "mid": v(349.5, -5.38) * mm, "end": v(348.98, -9.61) * mm});
            skArc(sketch, "E311", {"start": v(348.98, -9.61) * mm, "mid": v(347.4, -14.62) * mm, "end": v(345.2, -19.38) * mm});
            skArc(sketch, "E312", {"start": v(345.2, -19.38) * mm, "mid": v(341.45, -25.11) * mm, "end": v(336.82, -30.17) * mm});
            skArc(sketch, "E313", {"start": v(336.82, -30.17) * mm, "mid": v(331.13, -34.8) * mm, "end": v(324.88, -38.63) * mm});
            skArc(sketch, "E314", {"start": v(324.88, -38.63) * mm, "mid": v(317.36, -42.06) * mm, "end": v(309.5, -44.6) * mm});
            skArc(sketch, "E315", {"start": v(309.5, -44.6) * mm, "mid": v(300.24, -46.64) * mm, "end": v(290.87, -47.97) * mm});
            skArc(sketch, "E316", {"start": v(290.87, -47.97) * mm, "mid": v(285.36, -48.42) * mm, "end": v(279.83, -48.66) * mm});
            skArc(sketch, "E317", {"start": v(279.83, -48.66) * mm, "mid": v(269.64, -48.85) * mm, "end": v(259.46, -48.97) * mm});
            skArc(sketch, "E318", {"start": v(259.46, -48.97) * mm, "mid": v(248.1, -49.06) * mm, "end": v(236.73, -49.14) * mm});
            skArc(sketch, "E319", {"start": v(236.73, -49.14) * mm, "mid": v(236.21, -48.93) * mm, "end": v(236, -48.42) * mm});
            skArc(sketch, "E320", {"start": v(236, -48.42) * mm, "mid": v(236.02, -48.18) * mm, "end": v(236.1, -47.96) * mm});
            skArc(sketch, "E321", {"start": v(236.1, -47.96) * mm, "mid": v(239.81, -39.26) * mm, "end": v(243.53, -30.56) * mm});
            skArc(sketch, "E322", {"start": v(243.53, -30.56) * mm, "mid": v(247.67, -20.9) * mm, "end": v(251.81, -11.26) * mm});
            skArc(sketch, "E323", {"start": v(251.81, -11.26) * mm, "mid": v(256.72, 0.15) * mm, "end": v(261.64, 11.55) * mm});
            skLineSegment(sketch, "E324", {"start": v(261.64, 11.55) * mm, "end": v(287.29, 70.94) * mm});
            skLineSegment(sketch, "E325", {"start": v(287.29, 70.94) * mm, "end": v(297.9, 71.33) * mm});
            skArc(sketch, "E326", {"start": v(297.9, 71.33) * mm, "mid": v(305.67, 71.54) * mm, "end": v(313.45, 71.61) * mm});
            skArc(sketch, "E327", {"start": v(313.45, 71.61) * mm, "mid": v(321.46, 71.54) * mm, "end": v(329.48, 71.33) * mm});
            skArc(sketch, "E328", {"start": v(329.48, 71.33) * mm, "mid": v(336.52, 71.03) * mm, "end": v(343.57, 70.63) * mm});
            skArc(sketch, "E329", {"start": v(343.57, 70.63) * mm, "mid": v(347.06, 70.23) * mm, "end": v(350.5, 69.5) * mm});
            skArc(sketch, "E330", {"start": v(-372.67, 68.55) * mm, "mid": v(-368.39, 67.21) * mm, "end": v(-364.23, 65.53) * mm});
            skArc(sketch, "E331", {"start": v(-364.23, 65.53) * mm, "mid": v(-360.04, 63.46) * mm, "end": v(-356, 61.1) * mm});
            skArc(sketch, "E332", {"start": v(-356, 61.1) * mm, "mid": v(-352.71, 58.84) * mm, "end": v(-349.57, 56.37) * mm});
            skArc(sketch, "E333", {"start": v(-349.57, 56.37) * mm, "mid": v(-348.42, 54.81) * mm, "end": v(-348.08, 52.9) * mm});
            skArc(sketch, "E334", {"start": v(-348.08, 52.9) * mm, "mid": v(-348.19, 52.45) * mm, "end": v(-348.45, 52.05) * mm});
            skArc(sketch, "E335", {"start": v(-348.45, 52.05) * mm, "mid": v(-349.7, 50.7) * mm, "end": v(-350.96, 49.38) * mm});
            skArc(sketch, "E336", {"start": v(-350.96, 49.38) * mm, "mid": v(-352.5, 47.82) * mm, "end": v(-354.09, 46.29) * mm});
            skArc(sketch, "E337", {"start": v(-354.09, 46.29) * mm, "mid": v(-355.92, 44.57) * mm, "end": v(-357.78, 42.88) * mm});
            skLineSegment(sketch, "E338", {"start": v(-357.78, 42.88) * mm, "end": v(-367.4, 34.27) * mm});
            skLineSegment(sketch, "E339", {"start": v(-367.4, 34.27) * mm, "end": v(-372.44, 39.8) * mm});
            skArc(sketch, "E340", {"start": v(-372.44, 39.8) * mm, "mid": v(-374.7, 42.1) * mm, "end": v(-377.1, 44.24) * mm});
            skArc(sketch, "E341", {"start": v(-377.1, 44.24) * mm, "mid": v(-379.18, 45.76) * mm, "end": v(-381.44, 47) * mm});
            skArc(sketch, "E342", {"start": v(-381.44, 47) * mm, "mid": v(-383.76, 47.9) * mm, "end": v(-386.17, 48.46) * mm});
            skArc(sketch, "E343", {"start": v(-386.17, 48.46) * mm, "mid": v(-389.08, 48.8) * mm, "end": v(-392, 48.9) * mm});
            skArc(sketch, "E344", {"start": v(-392, 48.9) * mm, "mid": v(-394.6, 48.81) * mm, "end": v(-397.18, 48.6) * mm});
            skArc(sketch, "E345", {"start": v(-397.18, 48.6) * mm, "mid": v(-399.22, 48.26) * mm, "end": v(-401.23, 47.72) * mm});
            skArc(sketch, "E346", {"start": v(-401.23, 47.72) * mm, "mid": v(-403.17, 46.98) * mm, "end": v(-405.03, 46.06) * mm});
            skArc(sketch, "E347", {"start": v(-405.03, 46.06) * mm, "mid": v(-407.25, 44.73) * mm, "end": v(-409.4, 43.29) * mm});
            skArc(sketch, "E348", {"start": v(-409.4, 43.29) * mm, "mid": v(-413.14, 40.2) * mm, "end": v(-416.37, 36.58) * mm});
            skArc(sketch, "E349", {"start": v(-416.37, 36.58) * mm, "mid": v(-420.26, 31.15) * mm, "end": v(-423.83, 25.5) * mm});
            skArc(sketch, "E350", {"start": v(-423.83, 25.5) * mm, "mid": v(-427.33, 19.16) * mm, "end": v(-430.45, 12.63) * mm});
            skArc(sketch, "E351", {"start": v(-430.45, 12.63) * mm, "mid": v(-432.93, 6.4) * mm, "end": v(-434.94, 0.02) * mm});
            skArc(sketch, "E352", {"start": v(-434.94, 0.02) * mm, "mid": v(-435.74, -3.15) * mm, "end": v(-436.42, -6.35) * mm});
            skArc(sketch, "E353", {"start": v(-436.42, -6.35) * mm, "mid": v(-436.77, -8.81) * mm, "end": v(-436.9, -11.3) * mm});
            skArc(sketch, "E354", {"start": v(-436.9, -11.3) * mm, "mid": v(-436.79, -13.32) * mm, "end": v(-436.44, -15.3) * mm});
            skArc(sketch, "E355", {"start": v(-436.44, -15.3) * mm, "mid": v(-435.88, -17.05) * mm, "end": v(-435.05, -18.69) * mm});
            skArc(sketch, "E356", {"start": v(-435.05, -18.69) * mm, "mid": v(-433.56, -20.66) * mm, "end": v(-431.72, -22.3) * mm});
            skArc(sketch, "E357", {"start": v(-431.72, -22.3) * mm, "mid": v(-429.83, -23.27) * mm, "end": v(-427.75, -23.61) * mm});
            skArc(sketch, "E358", {"start": v(-427.75, -23.61) * mm, "mid": v(-425.33, -23.33) * mm, "end": v(-423.06, -22.47) * mm});
            skArc(sketch, "E359", {"start": v(-423.06, -22.47) * mm, "mid": v(-420.24, -20.8) * mm, "end": v(-417.6, -18.83) * mm});
            skArc(sketch, "E360", {"start": v(-417.6, -18.83) * mm, "mid": v(-415.99, -17.36) * mm, "end": v(-414.52, -15.74) * mm});
            skArc(sketch, "E361", {"start": v(-414.52, -15.74) * mm, "mid": v(-412.45, -13.13) * mm, "end": v(-410.46, -10.47) * mm});
            skArc(sketch, "E362", {"start": v(-410.46, -10.47) * mm, "mid": v(-408.53, -7.76) * mm, "end": v(-406.66, -5.01) * mm});
            skArc(sketch, "E363", {"start": v(-406.66, -5.01) * mm, "mid": v(-406.17, -3.98) * mm, "end": v(-406, -2.84) * mm});
            skArc(sketch, "E364", {"start": v(-406, -2.84) * mm, "mid": v(-406.08, -2.62) * mm, "end": v(-406.3, -2.5) * mm});
            skArc(sketch, "E365", {"start": v(-406.3, -2.5) * mm, "mid": v(-407.4, -2.37) * mm, "end": v(-408.5, -2.25) * mm});
            skArc(sketch, "E366", {"start": v(-408.5, -2.25) * mm, "mid": v(-409.87, -2.13) * mm, "end": v(-411.24, -2.06) * mm});
            skArc(sketch, "E367", {"start": v(-411.24, -2.06) * mm, "mid": v(-412.87, -2.02) * mm, "end": v(-414.5, -2) * mm});
            skArc(sketch, "E368", {"start": v(-414.5, -2) * mm, "mid": v(-416.13, -1.99) * mm, "end": v(-417.75, -1.95) * mm});
            skArc(sketch, "E369", {"start": v(-417.75, -1.95) * mm, "mid": v(-419.12, -1.88) * mm, "end": v(-420.48, -1.78) * mm});
            skArc(sketch, "E370", {"start": v(-420.48, -1.78) * mm, "mid": v(-421.58, -1.67) * mm, "end": v(-422.68, -1.55) * mm});
            skArc(sketch, "E371", {"start": v(-422.68, -1.55) * mm, "mid": v(-422.87, -1.45) * mm, "end": v(-422.92, -1.25) * mm});
            skArc(sketch, "E372", {"start": v(-422.92, -1.25) * mm, "mid": v(-422.87, -0.98) * mm, "end": v(-422.76, -0.73) * mm});
            skArc(sketch, "E373", {"start": v(-422.76, -0.73) * mm, "mid": v(-422.05, 0.52) * mm, "end": v(-421.33, 1.78) * mm});
            skArc(sketch, "E374", {"start": v(-421.33, 1.78) * mm, "mid": v(-420.48, 3.24) * mm, "end": v(-419.62, 4.69) * mm});
            skArc(sketch, "E375", {"start": v(-419.62, 4.69) * mm, "mid": v(-418.62, 6.35) * mm, "end": v(-417.6, 8) * mm});
            skLineSegment(sketch, "E376", {"start": v(-417.6, 8) * mm, "end": v(-412.36, 16.5) * mm});
            skLineSegment(sketch, "E377", {"start": v(-412.36, 16.5) * mm, "end": v(-390.06, 16.77) * mm});
            skArc(sketch, "E378", {"start": v(-390.06, 16.77) * mm, "mid": v(-384.28, 16.83) * mm, "end": v(-378.5, 16.86) * mm});
            skArc(sketch, "E379", {"start": v(-378.5, 16.86) * mm, "mid": v(-375.43, 16.83) * mm, "end": v(-372.36, 16.73) * mm});
            skArc(sketch, "E380", {"start": v(-372.36, 16.73) * mm, "mid": v(-370.51, 16.61) * mm, "end": v(-368.67, 16.44) * mm});
            skArc(sketch, "E381", {"start": v(-368.67, 16.44) * mm, "mid": v(-368.3, 16.2) * mm, "end": v(-368.26, 15.76) * mm});
            skArc(sketch, "E382", {"start": v(-368.26, 15.76) * mm, "mid": v(-368.43, 15.28) * mm, "end": v(-368.58, 14.8) * mm});
            skArc(sketch, "E383", {"start": v(-368.58, 14.8) * mm, "mid": v(-369.35, 12) * mm, "end": v(-370.11, 9.22) * mm});
            skArc(sketch, "E384", {"start": v(-370.11, 9.22) * mm, "mid": v(-371, 5.97) * mm, "end": v(-371.88, 2.73) * mm});
            skArc(sketch, "E385", {"start": v(-371.88, 2.73) * mm, "mid": v(-372.88, -1) * mm, "end": v(-373.88, -4.73) * mm});
            skArc(sketch, "E386", {"start": v(-373.88, -4.73) * mm, "mid": v(-375.66, -11.74) * mm, "end": v(-377.3, -18.79) * mm});
            skArc(sketch, "E387", {"start": v(-377.3, -18.79) * mm, "mid": v(-378.23, -23.77) * mm, "end": v(-378.85, -28.8) * mm});
            skArc(sketch, "E388", {"start": v(-378.85, -28.8) * mm, "mid": v(-379.05, -32.87) * mm, "end": v(-378.9, -36.94) * mm});
            skArc(sketch, "E389", {"start": v(-378.9, -36.94) * mm, "mid": v(-378.42, -40.88) * mm, "end": v(-377.57, -44.76) * mm});
            skArc(sketch, "E390", {"start": v(-377.57, -44.76) * mm, "mid": v(-375.65, -50.27) * mm, "end": v(-372.93, -55.43) * mm});
            skArc(sketch, "E391", {"start": v(-372.93, -55.43) * mm, "mid": v(-369.72, -59.48) * mm, "end": v(-365.72, -62.75) * mm});
            skArc(sketch, "E392", {"start": v(-365.72, -62.75) * mm, "mid": v(-360.77, -65.34) * mm, "end": v(-355.42, -66.94) * mm});
            skArc(sketch, "E393", {"start": v(-355.42, -66.94) * mm, "mid": v(-348.5, -67.96) * mm, "end": v(-341.5, -68.28) * mm});
            skArc(sketch, "E394", {"start": v(-341.5, -68.28) * mm, "mid": v(-337.4, -68.2) * mm, "end": v(-333.3, -67.99) * mm});
            skArc(sketch, "E395", {"start": v(-333.3, -67.99) * mm, "mid": v(-329.63, -67.65) * mm, "end": v(-325.98, -67.15) * mm});
            skArc(sketch, "E396", {"start": v(-325.98, -67.15) * mm, "mid": v(-322.05, -66.43) * mm, "end": v(-318.15, -65.55) * mm});
            skArc(sketch, "E397", {"start": v(-318.15, -65.55) * mm, "mid": v(-313.24, -64.3) * mm, "end": v(-308.35, -62.93) * mm});
            skArc(sketch, "E398", {"start": v(-308.35, -62.93) * mm, "mid": v(-306.38, -62.37) * mm, "end": v(-304.4, -61.8) * mm});
            skArc(sketch, "E399", {"start": v(-304.4, -61.8) * mm, "mid": v(-302.68, -61.33) * mm, "end": v(-300.95, -60.86) * mm});
            skArc(sketch, "E400", {"start": v(-300.95, -60.86) * mm, "mid": v(-299.47, -60.47) * mm, "end": v(-297.98, -60.07) * mm});
            skArc(sketch, "E401", {"start": v(-297.98, -60.07) * mm, "mid": v(-297.7, -60.02) * mm, "end": v(-297.4, -60) * mm});
            skArc(sketch, "E402", {"start": v(-297.4, -60) * mm, "mid": v(-297.06, -60.23) * mm, "end": v(-297.13, -60.64) * mm});
            skArc(sketch, "E403", {"start": v(-297.13, -60.64) * mm, "mid": v(-298.87, -62.41) * mm, "end": v(-300.65, -64.15) * mm});
            skArc(sketch, "E404", {"start": v(-300.65, -64.15) * mm, "mid": v(-302.84, -66.15) * mm, "end": v(-305.09, -68.08) * mm});
            skArc(sketch, "E405", {"start": v(-305.09, -68.08) * mm, "mid": v(-307.34, -69.89) * mm, "end": v(-309.65, -71.61) * mm});
            skArc(sketch, "E406", {"start": v(-309.65, -71.61) * mm, "mid": v(-313.08, -73.93) * mm, "end": v(-316.65, -76.04) * mm});
            skArc(sketch, "E407", {"start": v(-316.65, -76.04) * mm, "mid": v(-321.01, -78.36) * mm, "end": v(-325.46, -80.53) * mm});
            skArc(sketch, "E408", {"start": v(-325.46, -80.53) * mm, "mid": v(-330.04, -82.57) * mm, "end": v(-334.69, -84.45) * mm});
            skArc(sketch, "E409", {"start": v(-334.69, -84.45) * mm, "mid": v(-338.8, -85.92) * mm, "end": v(-343, -87.17) * mm});
            skArc(sketch, "E410", {"start": v(-343, -87.17) * mm, "mid": v(-347.78, -88.26) * mm, "end": v(-352.64, -89) * mm});
            skArc(sketch, "E411", {"start": v(-352.64, -89) * mm, "mid": v(-358.07, -89.45) * mm, "end": v(-363.52, -89.6) * mm});
            skArc(sketch, "E412", {"start": v(-363.52, -89.6) * mm, "mid": v(-368.64, -89.46) * mm, "end": v(-373.75, -89.03) * mm});
            skArc(sketch, "E413", {"start": v(-373.75, -89.03) * mm, "mid": v(-377.5, -88.35) * mm, "end": v(-381.15, -87.17) * mm});
            skArc(sketch, "E414", {"start": v(-381.15, -87.17) * mm, "mid": v(-386.35, -84.56) * mm, "end": v(-391.02, -81.08) * mm});
            skArc(sketch, "E415", {"start": v(-391.02, -81.08) * mm, "mid": v(-395.39, -76.6) * mm, "end": v(-399.09, -71.53) * mm});
            skArc(sketch, "E416", {"start": v(-399.09, -71.53) * mm, "mid": v(-402.33, -65.56) * mm, "end": v(-404.78, -59.22) * mm});
            skArc(sketch, "E417", {"start": v(-404.78, -59.22) * mm, "mid": v(-406.58, -52.2) * mm, "end": v(-407.63, -45.03) * mm});
            skLineSegment(sketch, "E418", {"start": v(-407.63, -45.03) * mm, "end": v(-408.28, -38.1) * mm});
            skLineSegment(sketch, "E419", {"start": v(-408.28, -38.1) * mm, "end": v(-411.58, -40.63) * mm});
            skArc(sketch, "E420", {"start": v(-411.58, -40.63) * mm, "mid": v(-417.58, -44.24) * mm, "end": v(-424.22, -46.47) * mm});
            skArc(sketch, "E421", {"start": v(-424.22, -46.47) * mm, "mid": v(-432.07, -47.57) * mm, "end": v(-439.99, -47.46) * mm});
            skArc(sketch, "E422", {"start": v(-439.99, -47.46) * mm, "mid": v(-447.78, -46.17) * mm, "end": v(-455.29, -43.7) * mm});
            skArc(sketch, "E423", {"start": v(-455.29, -43.7) * mm, "mid": v(-461.37, -40.34) * mm, "end": v(-466.56, -35.73) * mm});
            skArc(sketch, "E424", {"start": v(-466.56, -35.73) * mm, "mid": v(-468.57, -33.24) * mm, "end": v(-470.33, -30.57) * mm});
            skArc(sketch, "E425", {"start": v(-470.33, -30.57) * mm, "mid": v(-471.67, -27.93) * mm, "end": v(-472.66, -25.15) * mm});
            skArc(sketch, "E426", {"start": v(-472.66, -25.15) * mm, "mid": v(-473.38, -21.98) * mm, "end": v(-473.75, -18.75) * mm});
            skArc(sketch, "E427", {"start": v(-473.75, -18.75) * mm, "mid": v(-473.87, -14.66) * mm, "end": v(-473.76, -10.56) * mm});
            skArc(sketch, "E428", {"start": v(-473.76, -10.56) * mm, "mid": v(-473.6, -8.2) * mm, "end": v(-473.36, -5.85) * mm});
            skArc(sketch, "E429", {"start": v(-473.36, -5.85) * mm, "mid": v(-473.05, -3.65) * mm, "end": v(-472.67, -1.46) * mm});
            skArc(sketch, "E430", {"start": v(-472.67, -1.46) * mm, "mid": v(-472.19, 0.75) * mm, "end": v(-471.63, 2.95) * mm});
            skArc(sketch, "E431", {"start": v(-471.63, 2.95) * mm, "mid": v(-470.93, 5.35) * mm, "end": v(-470.16, 7.72) * mm});
            skArc(sketch, "E432", {"start": v(-470.16, 7.72) * mm, "mid": v(-465.5, 19.51) * mm, "end": v(-459.67, 30.76) * mm});
            skArc(sketch, "E433", {"start": v(-459.67, 30.76) * mm, "mid": v(-453.14, 40.38) * mm, "end": v(-445.4, 49.05) * mm});
            skArc(sketch, "E434", {"start": v(-445.4, 49.05) * mm, "mid": v(-437.01, 56.19) * mm, "end": v(-427.7, 62.06) * mm});
            skArc(sketch, "E435", {"start": v(-427.7, 62.06) * mm, "mid": v(-417.67, 66.55) * mm, "end": v(-407.1, 69.57) * mm});
            skArc(sketch, "E436", {"start": v(-407.1, 69.57) * mm, "mid": v(-403.48, 70.17) * mm, "end": v(-399.8, 70.47) * mm});
            skArc(sketch, "E437", {"start": v(-399.8, 70.47) * mm, "mid": v(-394.86, 70.58) * mm, "end": v(-389.9, 70.52) * mm});
            skArc(sketch, "E438", {"start": v(-389.9, 70.52) * mm, "mid": v(-384.94, 70.29) * mm, "end": v(-380, 69.88) * mm});
            skArc(sketch, "E439", {"start": v(-380, 69.88) * mm, "mid": v(-376.3, 69.36) * mm, "end": v(-372.67, 68.55) * mm});
            skArc(sketch, "E440", {"start": v(97.5, 44.53) * mm, "mid": v(100.4, 44.07) * mm, "end": v(103.23, 43.33) * mm});
            skArc(sketch, "E441", {"start": v(103.23, 43.33) * mm, "mid": v(105.88, 42.34) * mm, "end": v(108.42, 41.08) * mm});
            skArc(sketch, "E442", {"start": v(108.42, 41.08) * mm, "mid": v(110.65, 39.64) * mm, "end": v(112.7, 37.96) * mm});
            skArc(sketch, "E443", {"start": v(112.7, 37.96) * mm, "mid": v(114.36, 36.18) * mm, "end": v(115.74, 34.18) * mm});
            skArc(sketch, "E444", {"start": v(115.74, 34.18) * mm, "mid": v(116.5, 32.8) * mm, "end": v(117.18, 31.39) * mm});
            skArc(sketch, "E445", {"start": v(117.18, 31.39) * mm, "mid": v(117.64, 30.22) * mm, "end": v(117.98, 29) * mm});
            skArc(sketch, "E446", {"start": v(117.98, 29) * mm, "mid": v(118.22, 27.63) * mm, "end": v(118.35, 26.23) * mm});
            skArc(sketch, "E447", {"start": v(118.35, 26.23) * mm, "mid": v(118.42, 24.12) * mm, "end": v(118.44, 22) * mm});
            skArc(sketch, "E448", {"start": v(118.44, 22) * mm, "mid": v(117.9, 15.1) * mm, "end": v(116.37, 8.33) * mm});
            skArc(sketch, "E449", {"start": v(116.37, 8.33) * mm, "mid": v(113.66, 0.7) * mm, "end": v(110.26, -6.66) * mm});
            skArc(sketch, "E450", {"start": v(110.26, -6.66) * mm, "mid": v(106.03, -13.98) * mm, "end": v(101.18, -20.89) * mm});
            skArc(sketch, "E451", {"start": v(101.18, -20.89) * mm, "mid": v(96.01, -26.9) * mm, "end": v(90.23, -32.31) * mm});
            skArc(sketch, "E452", {"start": v(90.23, -32.31) * mm, "mid": v(87.36, -34.54) * mm, "end": v(84.33, -36.54) * mm});
            skArc(sketch, "E453", {"start": v(84.33, -36.54) * mm, "mid": v(80.33, -38.86) * mm, "end": v(76.24, -41.03) * mm});
            skArc(sketch, "E454", {"start": v(76.24, -41.03) * mm, "mid": v(72.08, -43.05) * mm, "end": v(67.85, -44.9) * mm});
            skArc(sketch, "E455", {"start": v(67.85, -44.9) * mm, "mid": v(64.47, -46.15) * mm, "end": v(61, -47.14) * mm});
            skArc(sketch, "E456", {"start": v(61, -47.14) * mm, "mid": v(57.45, -47.84) * mm, "end": v(53.85, -48.23) * mm});
            skArc(sketch, "E457", {"start": v(53.85, -48.23) * mm, "mid": v(49.17, -48.43) * mm, "end": v(44.47, -48.45) * mm});
            skArc(sketch, "E458", {"start": v(44.47, -48.45) * mm, "mid": v(39.9, -48.28) * mm, "end": v(35.33, -47.93) * mm});
            skArc(sketch, "E459", {"start": v(35.33, -47.93) * mm, "mid": v(32.2, -47.44) * mm, "end": v(29.16, -46.6) * mm});
            skArc(sketch, "E460", {"start": v(29.16, -46.6) * mm, "mid": v(27.13, -45.81) * mm, "end": v(25.18, -44.86) * mm});
            skArc(sketch, "E461", {"start": v(25.18, -44.86) * mm, "mid": v(23.17, -43.68) * mm, "end": v(21.24, -42.36) * mm});
            skArc(sketch, "E462", {"start": v(21.24, -42.36) * mm, "mid": v(19.54, -41.02) * mm, "end": v(17.94, -39.55) * mm});
            skArc(sketch, "E463", {"start": v(17.94, -39.55) * mm, "mid": v(16.84, -38.3) * mm, "end": v(15.94, -36.89) * mm});
            skArc(sketch, "E464", {"start": v(15.94, -36.89) * mm, "mid": v(14.26, -32.54) * mm, "end": v(13.67, -27.91) * mm});
            skArc(sketch, "E465", {"start": v(13.67, -27.91) * mm, "mid": v(13.98, -21.8) * mm, "end": v(14.96, -15.76) * mm});
            skArc(sketch, "E466", {"start": v(14.96, -15.76) * mm, "mid": v(16.82, -8.88) * mm, "end": v(19.35, -2.21) * mm});
            skArc(sketch, "E467", {"start": v(19.35, -2.21) * mm, "mid": v(22.65, 4.58) * mm, "end": v(26.49, 11.09) * mm});
            skArc(sketch, "E468", {"start": v(26.49, 11.09) * mm, "mid": v(31.48, 18.02) * mm, "end": v(37.13, 24.43) * mm});
            skArc(sketch, "E469", {"start": v(37.13, 24.43) * mm, "mid": v(43.12, 29.91) * mm, "end": v(49.7, 34.67) * mm});
            skArc(sketch, "E470", {"start": v(49.7, 34.67) * mm, "mid": v(56.61, 38.53) * mm, "end": v(63.94, 41.54) * mm});
            skArc(sketch, "E471", {"start": v(63.94, 41.54) * mm, "mid": v(71.62, 43.69) * mm, "end": v(79.5, 44.93) * mm});
            skArc(sketch, "E472", {"start": v(79.5, 44.93) * mm, "mid": v(81.83, 45.14) * mm, "end": v(84.16, 45.31) * mm});
            skArc(sketch, "E473", {"start": v(84.16, 45.31) * mm, "mid": v(85.84, 45.38) * mm, "end": v(87.52, 45.38) * mm});
            skArc(sketch, "E474", {"start": v(87.52, 45.38) * mm, "mid": v(89.38, 45.3) * mm, "end": v(91.24, 45.17) * mm});
            skArc(sketch, "E475", {"start": v(91.24, 45.17) * mm, "mid": v(94.37, 44.86) * mm, "end": v(97.5, 44.53) * mm});
            skArc(sketch, "E476", {"start": v(-484.88, 42.98) * mm, "mid": v(-480.67, 41.37) * mm, "end": v(-476.84, 38.98) * mm});
            skArc(sketch, "E477", {"start": v(-476.84, 38.98) * mm, "mid": v(-473.89, 36.09) * mm, "end": v(-471.72, 32.56) * mm});
            skArc(sketch, "E478", {"start": v(-471.72, 32.56) * mm, "mid": v(-470.41, 28.47) * mm, "end": v(-470.08, 24.2) * mm});
            skArc(sketch, "E479", {"start": v(-470.08, 24.2) * mm, "mid": v(-470.66, 19.35) * mm, "end": v(-472, 14.67) * mm});
            skArc(sketch, "E480", {"start": v(-472, 14.67) * mm, "mid": v(-474.67, 9.36) * mm, "end": v(-478.38, 4.72) * mm});
            skArc(sketch, "E481", {"start": v(-478.38, 4.72) * mm, "mid": v(-483.6, 0.07) * mm, "end": v(-489.38, -3.86) * mm});
            skArc(sketch, "E482", {"start": v(-489.38, -3.86) * mm, "mid": v(-496.54, -7.57) * mm, "end": v(-504.06, -10.45) * mm});
            skArc(sketch, "E483", {"start": v(-504.06, -10.45) * mm, "mid": v(-512.65, -12.82) * mm, "end": v(-521.4, -14.47) * mm});
            skArc(sketch, "E484", {"start": v(-521.4, -14.47) * mm, "mid": v(-524.08, -14.87) * mm, "end": v(-526.76, -15.3) * mm});
            skArc(sketch, "E485", {"start": v(-526.76, -15.3) * mm, "mid": v(-527.63, -15.52) * mm, "end": v(-528.46, -15.87) * mm});
            skArc(sketch, "E486", {"start": v(-528.46, -15.87) * mm, "mid": v(-528.92, -16.25) * mm, "end": v(-529.16, -16.8) * mm});
            skArc(sketch, "E487", {"start": v(-529.16, -16.8) * mm, "mid": v(-529.29, -17.68) * mm, "end": v(-529.29, -18.57) * mm});
            skArc(sketch, "E488", {"start": v(-529.29, -18.57) * mm, "mid": v(-529.2, -19.25) * mm, "end": v(-529.02, -19.9) * mm});
            skArc(sketch, "E489", {"start": v(-529.02, -19.9) * mm, "mid": v(-528.74, -20.62) * mm, "end": v(-528.4, -21.31) * mm});
            skArc(sketch, "E490", {"start": v(-528.4, -21.31) * mm, "mid": v(-528, -22) * mm, "end": v(-527.53, -22.65) * mm});
            skArc(sketch, "E491", {"start": v(-527.53, -22.65) * mm, "mid": v(-527.03, -23.22) * mm, "end": v(-526.48, -23.75) * mm});
            skArc(sketch, "E492", {"start": v(-526.48, -23.75) * mm, "mid": v(-524.69, -24.92) * mm, "end": v(-522.64, -25.55) * mm});
            skArc(sketch, "E493", {"start": v(-522.64, -25.55) * mm, "mid": v(-519.42, -25.95) * mm, "end": v(-516.17, -26.06) * mm});
            skArc(sketch, "E494", {"start": v(-516.17, -26.06) * mm, "mid": v(-512.06, -25.9) * mm, "end": v(-507.97, -25.43) * mm});
            skArc(sketch, "E495", {"start": v(-507.97, -25.43) * mm, "mid": v(-503.22, -24.6) * mm, "end": v(-498.5, -23.58) * mm});
            skArc(sketch, "E496", {"start": v(-498.5, -23.58) * mm, "mid": v(-496.58, -23.12) * mm, "end": v(-494.66, -22.66) * mm});
            skArc(sketch, "E497", {"start": v(-494.66, -22.66) * mm, "mid": v(-493.02, -22.3) * mm, "end": v(-491.38, -21.93) * mm});
            skArc(sketch, "E498", {"start": v(-491.38, -21.93) * mm, "mid": v(-489.94, -21.62) * mm, "end": v(-488.5, -21.3) * mm});
            skArc(sketch, "E499", {"start": v(-488.5, -21.3) * mm, "mid": v(-488.4, -21.3) * mm, "end": v(-488.3, -21.36) * mm});
            skArc(sketch, "E500", {"start": v(-488.3, -21.36) * mm, "mid": v(-488.24, -21.45) * mm, "end": v(-488.22, -21.55) * mm});
            skArc(sketch, "E501", {"start": v(-488.22, -21.55) * mm, "mid": v(-488.09, -22.85) * mm, "end": v(-487.96, -24.15) * mm});
            skArc(sketch, "E502", {"start": v(-487.96, -24.15) * mm, "mid": v(-487.83, -25.62) * mm, "end": v(-487.7, -27.1) * mm});
            skArc(sketch, "E503", {"start": v(-487.7, -27.1) * mm, "mid": v(-487.56, -28.83) * mm, "end": v(-487.43, -30.56) * mm});
            skLineSegment(sketch, "E504", {"start": v(-487.43, -30.56) * mm, "end": v(-486.75, -39.56) * mm});
            skLineSegment(sketch, "E505", {"start": v(-486.75, -39.56) * mm, "end": v(-489.37, -40.76) * mm});
            skArc(sketch, "E506", {"start": v(-489.37, -40.76) * mm, "mid": v(-493.5, -42.4) * mm, "end": v(-497.77, -43.64) * mm});
            skArc(sketch, "E507", {"start": v(-497.77, -43.64) * mm, "mid": v(-503.86, -44.96) * mm, "end": v(-510, -46.07) * mm});
            skArc(sketch, "E508", {"start": v(-510, -46.07) * mm, "mid": v(-516.3, -46.96) * mm, "end": v(-522.61, -47.62) * mm});
            skArc(sketch, "E509", {"start": v(-522.61, -47.62) * mm, "mid": v(-527.53, -47.86) * mm, "end": v(-532.45, -47.7) * mm});
            skArc(sketch, "E510", {"start": v(-532.45, -47.7) * mm, "mid": v(-537.74, -47.07) * mm, "end": v(-542.94, -45.93) * mm});
            skArc(sketch, "E511", {"start": v(-542.94, -45.93) * mm, "mid": v(-547.45, -44.37) * mm, "end": v(-551.72, -42.23) * mm});
            skArc(sketch, "E512", {"start": v(-551.72, -42.23) * mm, "mid": v(-555.14, -39.82) * mm, "end": v(-558.15, -36.91) * mm});
            skArc(sketch, "E513", {"start": v(-558.15, -36.91) * mm, "mid": v(-560.31, -33.85) * mm, "end": v(-561.77, -30.38) * mm});
            skArc(sketch, "E514", {"start": v(-561.77, -30.38) * mm, "mid": v(-562.42, -27.71) * mm, "end": v(-562.77, -24.99) * mm});
            skArc(sketch, "E515", {"start": v(-562.77, -24.99) * mm, "mid": v(-562.95, -21.52) * mm, "end": v(-562.94, -18.05) * mm});
            skArc(sketch, "E516", {"start": v(-562.94, -18.05) * mm, "mid": v(-562.73, -14.39) * mm, "end": v(-562.33, -10.74) * mm});
            skArc(sketch, "E517", {"start": v(-562.33, -10.74) * mm, "mid": v(-561.76, -7.42) * mm, "end": v(-560.97, -4.15) * mm});
            skArc(sketch, "E518", {"start": v(-560.97, -4.15) * mm, "mid": v(-557.3, 6.12) * mm, "end": v(-552.14, 15.74) * mm});
            skArc(sketch, "E519", {"start": v(-552.14, 15.74) * mm, "mid": v(-545.86, 23.97) * mm, "end": v(-538.25, 31) * mm});
            skArc(sketch, "E520", {"start": v(-538.25, 31) * mm, "mid": v(-529.6, 36.58) * mm, "end": v(-520.13, 40.57) * mm});
            skArc(sketch, "E521", {"start": v(-520.13, 40.57) * mm, "mid": v(-509.7, 43.07) * mm, "end": v(-499, 43.94) * mm});
            skArc(sketch, "E522", {"start": v(-499, 43.94) * mm, "mid": v(-496.86, 43.93) * mm, "end": v(-494.71, 43.89) * mm});
            skArc(sketch, "E523", {"start": v(-494.71, 43.89) * mm, "mid": v(-492.62, 43.8) * mm, "end": v(-490.52, 43.68) * mm});
            skArc(sketch, "E524", {"start": v(-490.52, 43.68) * mm, "mid": v(-488.72, 43.54) * mm, "end": v(-486.92, 43.37) * mm});
            skArc(sketch, "E525", {"start": v(-486.92, 43.37) * mm, "mid": v(-485.9, 43.22) * mm, "end": v(-484.88, 42.98) * mm});
            skArc(sketch, "E526", {"start": v(-293.43, 42.92) * mm, "mid": v(-289.14, 41.86) * mm, "end": v(-285.02, 40.27) * mm});
            skArc(sketch, "E527", {"start": v(-285.02, 40.27) * mm, "mid": v(-281.83, 38.38) * mm, "end": v(-279.12, 35.86) * mm});
            skArc(sketch, "E528", {"start": v(-279.12, 35.86) * mm, "mid": v(-277.14, 33) * mm, "end": v(-275.88, 29.75) * mm});
            skArc(sketch, "E529", {"start": v(-275.88, 29.75) * mm, "mid": v(-275.24, 25.95) * mm, "end": v(-275.26, 22.1) * mm});
            skArc(sketch, "E530", {"start": v(-275.26, 22.1) * mm, "mid": v(-276.72, 15.37) * mm, "end": v(-279.8, 9.2) * mm});
            skArc(sketch, "E531", {"start": v(-279.8, 9.2) * mm, "mid": v(-284.64, 3.18) * mm, "end": v(-290.46, -1.9) * mm});
            skArc(sketch, "E532", {"start": v(-290.46, -1.9) * mm, "mid": v(-298.14, -6.66) * mm, "end": v(-306.44, -10.26) * mm});
            skArc(sketch, "E533", {"start": v(-306.44, -10.26) * mm, "mid": v(-316.33, -13.18) * mm, "end": v(-326.47, -15.1) * mm});
            skArc(sketch, "E534", {"start": v(-326.47, -15.1) * mm, "mid": v(-329.54, -15.58) * mm, "end": v(-332.6, -16.13) * mm});
            skArc(sketch, "E535", {"start": v(-332.6, -16.13) * mm, "mid": v(-333.7, -16.54) * mm, "end": v(-334.6, -17.29) * mm});
            skArc(sketch, "E536", {"start": v(-334.6, -17.29) * mm, "mid": v(-335, -18.15) * mm, "end": v(-334.89, -19.1) * mm});
            skArc(sketch, "E537", {"start": v(-334.89, -19.1) * mm, "mid": v(-334.03, -20.93) * mm, "end": v(-333.04, -22.7) * mm});
            skArc(sketch, "E538", {"start": v(-333.04, -22.7) * mm, "mid": v(-332.52, -23.48) * mm, "end": v(-331.93, -24.22) * mm});
            skArc(sketch, "E539", {"start": v(-331.93, -24.22) * mm, "mid": v(-331.35, -24.8) * mm, "end": v(-330.7, -25.32) * mm});
            skArc(sketch, "E540", {"start": v(-330.7, -25.32) * mm, "mid": v(-330, -25.74) * mm, "end": v(-329.24, -26.08) * mm});
            skArc(sketch, "E541", {"start": v(-329.24, -26.08) * mm, "mid": v(-328.35, -26.37) * mm, "end": v(-327.43, -26.58) * mm});
            skArc(sketch, "E542", {"start": v(-327.43, -26.58) * mm, "mid": v(-325.33, -26.87) * mm, "end": v(-323.22, -26.94) * mm});
            skArc(sketch, "E543", {"start": v(-323.22, -26.94) * mm, "mid": v(-320.3, -26.84) * mm, "end": v(-317.4, -26.63) * mm});
            skArc(sketch, "E544", {"start": v(-317.4, -26.63) * mm, "mid": v(-314.21, -26.27) * mm, "end": v(-311.04, -25.8) * mm});
            skArc(sketch, "E545", {"start": v(-311.04, -25.8) * mm, "mid": v(-307.99, -25.2) * mm, "end": v(-304.97, -24.5) * mm});
            skArc(sketch, "E546", {"start": v(-304.97, -24.5) * mm, "mid": v(-303.76, -24.19) * mm, "end": v(-302.55, -23.9) * mm});
            skArc(sketch, "E547", {"start": v(-302.55, -23.9) * mm, "mid": v(-301.46, -23.67) * mm, "end": v(-300.36, -23.45) * mm});
            skArc(sketch, "E548", {"start": v(-300.36, -23.45) * mm, "mid": v(-299.45, -23.3) * mm, "end": v(-298.54, -23.14) * mm});
            skArc(sketch, "E549", {"start": v(-298.54, -23.14) * mm, "mid": v(-298.24, -23.13) * mm, "end": v(-297.94, -23.2) * mm});
            skArc(sketch, "E550", {"start": v(-297.94, -23.2) * mm, "mid": v(-297.65, -23.46) * mm, "end": v(-297.64, -23.86) * mm});
            skArc(sketch, "E551", {"start": v(-297.64, -23.86) * mm, "mid": v(-299.49, -28.68) * mm, "end": v(-301.35, -33.5) * mm});
            skArc(sketch, "E552", {"start": v(-301.35, -33.5) * mm, "mid": v(-303.14, -38.07) * mm, "end": v(-304.96, -42.64) * mm});
            skArc(sketch, "E553", {"start": v(-304.96, -42.64) * mm, "mid": v(-305.51, -43.68) * mm, "end": v(-306.25, -44.59) * mm});
            skArc(sketch, "E554", {"start": v(-306.25, -44.59) * mm, "mid": v(-307.2, -45.28) * mm, "end": v(-308.31, -45.65) * mm});
            skArc(sketch, "E555", {"start": v(-308.31, -45.65) * mm, "mid": v(-312.36, -46.29) * mm, "end": v(-316.42, -46.87) * mm});
            skArc(sketch, "E556", {"start": v(-316.42, -46.87) * mm, "mid": v(-320.67, -47.4) * mm, "end": v(-324.94, -47.82) * mm});
            skArc(sketch, "E557", {"start": v(-324.94, -47.82) * mm, "mid": v(-328.56, -48.06) * mm, "end": v(-332.19, -48.14) * mm});
            skArc(sketch, "E558", {"start": v(-332.19, -48.14) * mm, "mid": v(-336.34, -48.08) * mm, "end": v(-340.49, -47.84) * mm});
            skArc(sketch, "E559", {"start": v(-340.49, -47.84) * mm, "mid": v(-343.8, -47.47) * mm, "end": v(-347.06, -46.84) * mm});
            skArc(sketch, "E560", {"start": v(-347.06, -46.84) * mm, "mid": v(-349.93, -46.04) * mm, "end": v(-352.71, -45) * mm});
            skArc(sketch, "E561", {"start": v(-352.71, -45) * mm, "mid": v(-355.48, -43.68) * mm, "end": v(-358.13, -42.14) * mm});
            skArc(sketch, "E562", {"start": v(-358.13, -42.14) * mm, "mid": v(-362.28, -38.6) * mm, "end": v(-365.3, -34.05) * mm});
            skArc(sketch, "E563", {"start": v(-365.3, -34.05) * mm, "mid": v(-367.4, -28.27) * mm, "end": v(-368.33, -22.2) * mm});
            skArc(sketch, "E564", {"start": v(-368.33, -22.2) * mm, "mid": v(-368.16, -14.78) * mm, "end": v(-366.84, -7.47) * mm});
            skArc(sketch, "E565", {"start": v(-366.84, -7.47) * mm, "mid": v(-364.24, 0.83) * mm, "end": v(-360.86, 8.85) * mm});
            skArc(sketch, "E566", {"start": v(-360.86, 8.85) * mm, "mid": v(-355.82, 17.37) * mm, "end": v(-349.4, 24.9) * mm});
            skArc(sketch, "E567", {"start": v(-349.4, 24.9) * mm, "mid": v(-341.57, 31.5) * mm, "end": v(-332.81, 36.82) * mm});
            skArc(sketch, "E568", {"start": v(-332.81, 36.82) * mm, "mid": v(-323.3, 40.73) * mm, "end": v(-313.32, 43.13) * mm});
            skArc(sketch, "E569", {"start": v(-313.32, 43.13) * mm, "mid": v(-303.37, 43.87) * mm, "end": v(-293.43, 42.92) * mm});
            skArc(sketch, "E570", {"start": v(-241.1, 40.85) * mm, "mid": v(-240.86, 40.1) * mm, "end": v(-240.68, 39.34) * mm});
            skArc(sketch, "E571", {"start": v(-240.68, 39.34) * mm, "mid": v(-240.48, 38.35) * mm, "end": v(-240.32, 37.36) * mm});
            skArc(sketch, "E572", {"start": v(-240.32, 37.36) * mm, "mid": v(-240.19, 36.32) * mm, "end": v(-240.08, 35.27) * mm});
            skArc(sketch, "E573", {"start": v(-240.08, 35.27) * mm, "mid": v(-240.02, 34.33) * mm, "end": v(-240, 33.4) * mm});
            skLineSegment(sketch, "E574", {"start": v(-240, 33.4) * mm, "end": v(-240, 29.09) * mm});
            skLineSegment(sketch, "E575", {"start": v(-240, 29.09) * mm, "end": v(-232.65, 34.36) * mm});
            skArc(sketch, "E576", {"start": v(-232.65, 34.36) * mm, "mid": v(-229.34, 36.59) * mm, "end": v(-225.9, 38.62) * mm});
            skArc(sketch, "E577", {"start": v(-225.9, 38.62) * mm, "mid": v(-222.8, 40.16) * mm, "end": v(-219.56, 41.4) * mm});
            skArc(sketch, "E578", {"start": v(-219.56, 41.4) * mm, "mid": v(-216.3, 42.34) * mm, "end": v(-212.97, 42.96) * mm});
            skArc(sketch, "E579", {"start": v(-212.97, 42.96) * mm, "mid": v(-209.24, 43.35) * mm, "end": v(-205.5, 43.49) * mm});
            skArc(sketch, "E580", {"start": v(-205.5, 43.49) * mm, "mid": v(-201.5, 43.45) * mm, "end": v(-197.5, 43.33) * mm});
            skArc(sketch, "E581", {"start": v(-197.5, 43.33) * mm, "mid": v(-196.4, 43.03) * mm, "end": v(-195.57, 42.26) * mm});
            skArc(sketch, "E582", {"start": v(-195.57, 42.26) * mm, "mid": v(-195.36, 41.34) * mm, "end": v(-195.8, 40.5) * mm});
            skArc(sketch, "E583", {"start": v(-195.8, 40.5) * mm, "mid": v(-198.26, 38.45) * mm, "end": v(-200.8, 36.49) * mm});
            skArc(sketch, "E584", {"start": v(-200.8, 36.49) * mm, "mid": v(-202.42, 35.22) * mm, "end": v(-203.98, 33.89) * mm});
            skArc(sketch, "E585", {"start": v(-203.98, 33.89) * mm, "mid": v(-205.58, 32.4) * mm, "end": v(-207.13, 30.84) * mm});
            skArc(sketch, "E586", {"start": v(-207.13, 30.84) * mm, "mid": v(-208.66, 29.2) * mm, "end": v(-210.13, 27.5) * mm});
            skArc(sketch, "E587", {"start": v(-210.13, 27.5) * mm, "mid": v(-211.52, 25.78) * mm, "end": v(-212.83, 24) * mm});
            skArc(sketch, "E588", {"start": v(-212.83, 24) * mm, "mid": v(-214.45, 21.78) * mm, "end": v(-216.1, 19.58) * mm});
            skArc(sketch, "E589", {"start": v(-216.1, 19.58) * mm, "mid": v(-217, 18.52) * mm, "end": v(-218.01, 17.57) * mm});
            skArc(sketch, "E590", {"start": v(-218.01, 17.57) * mm, "mid": v(-218.9, 16.95) * mm, "end": v(-219.86, 16.5) * mm});
            skArc(sketch, "E591", {"start": v(-219.86, 16.5) * mm, "mid": v(-221.14, 16.12) * mm, "end": v(-222.44, 15.85) * mm});
            skArc(sketch, "E592", {"start": v(-222.44, 15.85) * mm, "mid": v(-224.55, 15.44) * mm, "end": v(-226.61, 14.86) * mm});
            skArc(sketch, "E593", {"start": v(-226.61, 14.86) * mm, "mid": v(-228.52, 14.13) * mm, "end": v(-230.34, 13.22) * mm});
            skArc(sketch, "E594", {"start": v(-230.34, 13.22) * mm, "mid": v(-232.2, 12.05) * mm, "end": v(-233.97, 10.72) * mm});
            skArc(sketch, "E595", {"start": v(-233.97, 10.72) * mm, "mid": v(-235.97, 8.99) * mm, "end": v(-237.88, 7.15) * mm});
            skArc(sketch, "E596", {"start": v(-237.88, 7.15) * mm, "mid": v(-239.42, 5.44) * mm, "end": v(-240.8, 3.6) * mm});
            skArc(sketch, "E597", {"start": v(-240.8, 3.6) * mm, "mid": v(-242.21, 1.36) * mm, "end": v(-243.49, -0.96) * mm});
            skArc(sketch, "E598", {"start": v(-243.49, -0.96) * mm, "mid": v(-245.25, -4.55) * mm, "end": v(-246.9, -8.2) * mm});
            skArc(sketch, "E599", {"start": v(-246.9, -8.2) * mm, "mid": v(-249.98, -15.34) * mm, "end": v(-253.02, -22.5) * mm});
            skLineSegment(sketch, "E600", {"start": v(-253.02, -22.5) * mm, "end": v(-263.56, -47.5) * mm});
            skLineSegment(sketch, "E601", {"start": v(-263.56, -47.5) * mm, "end": v(-279.9, -47.78) * mm});
            skArc(sketch, "E602", {"start": v(-279.9, -47.78) * mm, "mid": v(-284.1, -47.83) * mm, "end": v(-288.32, -47.87) * mm});
            skArc(sketch, "E603", {"start": v(-288.32, -47.87) * mm, "mid": v(-290.57, -47.84) * mm, "end": v(-292.8, -47.74) * mm});
            skArc(sketch, "E604", {"start": v(-292.8, -47.74) * mm, "mid": v(-294.08, -47.62) * mm, "end": v(-295.35, -47.43) * mm});
            skArc(sketch, "E605", {"start": v(-295.35, -47.43) * mm, "mid": v(-295.68, -47.19) * mm, "end": v(-295.7, -46.78) * mm});
            skArc(sketch, "E606", {"start": v(-295.7, -46.78) * mm, "mid": v(-295.5, -46.29) * mm, "end": v(-295.3, -45.8) * mm});
            skArc(sketch, "E607", {"start": v(-295.3, -45.8) * mm, "mid": v(-293.76, -42.18) * mm, "end": v(-292.21, -38.56) * mm});
            skArc(sketch, "E608", {"start": v(-292.21, -38.56) * mm, "mid": v(-290.44, -34.4) * mm, "end": v(-288.67, -30.23) * mm});
            skArc(sketch, "E609", {"start": v(-288.67, -30.23) * mm, "mid": v(-286.62, -25.4) * mm, "end": v(-284.57, -20.59) * mm});
            skArc(sketch, "E610", {"start": v(-284.57, -20.59) * mm, "mid": v(-282.45, -15.58) * mm, "end": v(-280.36, -10.56) * mm});
            skArc(sketch, "E611", {"start": v(-280.36, -10.56) * mm, "mid": v(-278.4, -5.8) * mm, "end": v(-276.48, -1.02) * mm});
            skArc(sketch, "E612", {"start": v(-276.48, -1.02) * mm, "mid": v(-274.87, 3.02) * mm, "end": v(-273.3, 7.07) * mm});
            skArc(sketch, "E613", {"start": v(-273.3, 7.07) * mm, "mid": v(-272.57, 9.04) * mm, "end": v(-271.92, 11.03) * mm});
            skArc(sketch, "E614", {"start": v(-271.92, 11.03) * mm, "mid": v(-271.16, 13.87) * mm, "end": v(-270.57, 16.75) * mm});
            skArc(sketch, "E615", {"start": v(-270.57, 16.75) * mm, "mid": v(-270.11, 19.92) * mm, "end": v(-269.8, 23.12) * mm});
            skArc(sketch, "E616", {"start": v(-269.8, 23.12) * mm, "mid": v(-269.66, 26.12) * mm, "end": v(-269.67, 29.12) * mm});
            skArc(sketch, "E617", {"start": v(-269.67, 29.12) * mm, "mid": v(-269.86, 31.39) * mm, "end": v(-270.3, 33.62) * mm});
            skLineSegment(sketch, "E618", {"start": v(-270.3, 33.62) * mm, "end": v(-271.1, 36.74) * mm});
            skLineSegment(sketch, "E619", {"start": v(-271.1, 36.74) * mm, "end": v(-257.3, 40.28) * mm});
            skArc(sketch, "E620", {"start": v(-257.3, 40.28) * mm, "mid": v(-254.63, 40.96) * mm, "end": v(-251.96, 41.64) * mm});
            skArc(sketch, "E621", {"start": v(-251.96, 41.64) * mm, "mid": v(-249.66, 42.22) * mm, "end": v(-247.36, 42.8) * mm});
            skArc(sketch, "E622", {"start": v(-247.36, 42.8) * mm, "mid": v(-245.35, 43.3) * mm, "end": v(-243.35, 43.8) * mm});
            skArc(sketch, "E623", {"start": v(-243.35, 43.8) * mm, "mid": v(-243.1, 43.86) * mm, "end": v(-242.85, 43.9) * mm});
            skArc(sketch, "E624", {"start": v(-242.85, 43.9) * mm, "mid": v(-242.67, 43.88) * mm, "end": v(-242.53, 43.77) * mm});
            skArc(sketch, "E625", {"start": v(-242.53, 43.77) * mm, "mid": v(-242.29, 43.42) * mm, "end": v(-242.06, 43.05) * mm});
            skArc(sketch, "E626", {"start": v(-242.06, 43.05) * mm, "mid": v(-241.8, 42.56) * mm, "end": v(-241.57, 42.05) * mm});
            skArc(sketch, "E627", {"start": v(-241.57, 42.05) * mm, "mid": v(-241.32, 41.46) * mm, "end": v(-241.1, 40.85) * mm});
            skArc(sketch, "E628", {"start": v(-138.8, 41.48) * mm, "mid": v(-133.82, 38.85) * mm, "end": v(-129.86, 34.86) * mm});
            skArc(sketch, "E629", {"start": v(-129.86, 34.86) * mm, "mid": v(-127.26, 29.86) * mm, "end": v(-126.27, 24.32) * mm});
            skArc(sketch, "E630", {"start": v(-126.27, 24.32) * mm, "mid": v(-126.9, 18.01) * mm, "end": v(-129.09, 12.06) * mm});
            skArc(sketch, "E631", {"start": v(-129.09, 12.06) * mm, "mid": v(-132.9, 6.13) * mm, "end": v(-137.72, 1.01) * mm});
            skArc(sketch, "E632", {"start": v(-137.72, 1.01) * mm, "mid": v(-141.53, -1.97) * mm, "end": v(-145.64, -4.52) * mm});
            skArc(sketch, "E633", {"start": v(-145.64, -4.52) * mm, "mid": v(-150.88, -7.15) * mm, "end": v(-156.27, -9.45) * mm});
            skArc(sketch, "E634", {"start": v(-156.27, -9.45) * mm, "mid": v(-162.2, -11.55) * mm, "end": v(-168.24, -13.3) * mm});
            skArc(sketch, "E635", {"start": v(-168.24, -13.3) * mm, "mid": v(-174.2, -14.62) * mm, "end": v(-180.25, -15.54) * mm});
            skArc(sketch, "E636", {"start": v(-180.25, -15.54) * mm, "mid": v(-181.92, -15.76) * mm, "end": v(-183.6, -16.01) * mm});
            skArc(sketch, "E637", {"start": v(-183.6, -16.01) * mm, "mid": v(-184.35, -16.2) * mm, "end": v(-185.06, -16.5) * mm});
            skArc(sketch, "E638", {"start": v(-185.06, -16.5) * mm, "mid": v(-185.48, -16.82) * mm, "end": v(-185.75, -17.27) * mm});
            skArc(sketch, "E639", {"start": v(-185.75, -17.27) * mm, "mid": v(-185.94, -17.9) * mm, "end": v(-186, -18.56) * mm});
            skArc(sketch, "E640", {"start": v(-186, -18.56) * mm, "mid": v(-185.96, -19.1) * mm, "end": v(-185.83, -19.65) * mm});
            skArc(sketch, "E641", {"start": v(-185.83, -19.65) * mm, "mid": v(-185.6, -20.33) * mm, "end": v(-185.3, -21) * mm});
            skArc(sketch, "E642", {"start": v(-185.3, -21) * mm, "mid": v(-184.95, -21.72) * mm, "end": v(-184.55, -22.4) * mm});
            skArc(sketch, "E643", {"start": v(-184.55, -22.4) * mm, "mid": v(-184.12, -23.03) * mm, "end": v(-183.65, -23.62) * mm});
            skArc(sketch, "E644", {"start": v(-183.65, -23.62) * mm, "mid": v(-182.12, -24.98) * mm, "end": v(-180.28, -25.88) * mm});
            skArc(sketch, "E645", {"start": v(-180.28, -25.88) * mm, "mid": v(-177.74, -26.54) * mm, "end": v(-175.14, -26.87) * mm});
            skArc(sketch, "E646", {"start": v(-175.14, -26.87) * mm, "mid": v(-171.63, -26.9) * mm, "end": v(-168.14, -26.62) * mm});
            skArc(sketch, "E647", {"start": v(-168.14, -26.62) * mm, "mid": v(-163.55, -25.93) * mm, "end": v(-158.99, -25.05) * mm});
            skArc(sketch, "E648", {"start": v(-158.99, -25.05) * mm, "mid": v(-157.03, -24.63) * mm, "end": v(-155.06, -24.24) * mm});
            skArc(sketch, "E649", {"start": v(-155.06, -24.24) * mm, "mid": v(-153.37, -23.91) * mm, "end": v(-151.69, -23.61) * mm});
            skArc(sketch, "E650", {"start": v(-151.69, -23.61) * mm, "mid": v(-150.23, -23.37) * mm, "end": v(-148.77, -23.12) * mm});
            skArc(sketch, "E651", {"start": v(-148.77, -23.12) * mm, "mid": v(-148.6, -23.14) * mm, "end": v(-148.44, -23.23) * mm});
            skArc(sketch, "E652", {"start": v(-148.44, -23.23) * mm, "mid": v(-148.37, -23.38) * mm, "end": v(-148.43, -23.53) * mm});
            skArc(sketch, "E653", {"start": v(-148.43, -23.53) * mm, "mid": v(-150.1, -25.31) * mm, "end": v(-151.79, -27.1) * mm});
            skArc(sketch, "E654", {"start": v(-151.79, -27.1) * mm, "mid": v(-153.72, -29.12) * mm, "end": v(-155.67, -31.13) * mm});
            skArc(sketch, "E655", {"start": v(-155.67, -31.13) * mm, "mid": v(-158, -33.5) * mm, "end": v(-160.36, -35.86) * mm});
            skLineSegment(sketch, "E656", {"start": v(-160.36, -35.86) * mm, "end": v(-172.65, -48.12) * mm});
            skLineSegment(sketch, "E657", {"start": v(-172.65, -48.12) * mm, "end": v(-183.57, -48.11) * mm});
            skArc(sketch, "E658", {"start": v(-183.57, -48.11) * mm, "mid": v(-193.4, -47.4) * mm, "end": v(-203, -45.32) * mm});
            skArc(sketch, "E659", {"start": v(-203, -45.32) * mm, "mid": v(-209.71, -42.13) * mm, "end": v(-215.06, -36.98) * mm});
            skArc(sketch, "E660", {"start": v(-215.06, -36.98) * mm, "mid": v(-218.53, -30.41) * mm, "end": v(-219.74, -23.09) * mm});
            skArc(sketch, "E661", {"start": v(-219.74, -23.09) * mm, "mid": v(-219.09, -13.26) * mm, "end": v(-217.05, -3.63) * mm});
            skArc(sketch, "E662", {"start": v(-217.05, -3.63) * mm, "mid": v(-215.73, 0.53) * mm, "end": v(-214.2, 4.63) * mm});
            skArc(sketch, "E663", {"start": v(-214.2, 4.63) * mm, "mid": v(-212.61, 8.18) * mm, "end": v(-210.77, 11.62) * mm});
            skArc(sketch, "E664", {"start": v(-210.77, 11.62) * mm, "mid": v(-208.67, 14.91) * mm, "end": v(-206.34, 18.05) * mm});
            skArc(sketch, "E665", {"start": v(-206.34, 18.05) * mm, "mid": v(-203.5, 21.41) * mm, "end": v(-200.5, 24.62) * mm});
            skArc(sketch, "E666", {"start": v(-200.5, 24.62) * mm, "mid": v(-198.28, 26.82) * mm, "end": v(-196.02, 28.96) * mm});
            skArc(sketch, "E667", {"start": v(-196.02, 28.96) * mm, "mid": v(-194.25, 30.5) * mm, "end": v(-192.4, 31.95) * mm});
            skArc(sketch, "E668", {"start": v(-192.4, 31.95) * mm, "mid": v(-190.59, 33.2) * mm, "end": v(-188.7, 34.34) * mm});
            skArc(sketch, "E669", {"start": v(-188.7, 34.34) * mm, "mid": v(-186.37, 35.6) * mm, "end": v(-184, 36.79) * mm});
            skArc(sketch, "E670", {"start": v(-184, 36.79) * mm, "mid": v(-182.18, 37.62) * mm, "end": v(-180.34, 38.41) * mm});
            skArc(sketch, "E671", {"start": v(-180.34, 38.41) * mm, "mid": v(-178.37, 39.2) * mm, "end": v(-176.38, 39.96) * mm});
            skArc(sketch, "E672", {"start": v(-176.38, 39.96) * mm, "mid": v(-174.55, 40.6) * mm, "end": v(-172.7, 41.22) * mm});
            skArc(sketch, "E673", {"start": v(-172.7, 41.22) * mm, "mid": v(-171.36, 41.6) * mm, "end": v(-170, 41.9) * mm});
            skArc(sketch, "E674", {"start": v(-170, 41.9) * mm, "mid": v(-168.87, 42.13) * mm, "end": v(-167.75, 42.35) * mm});
            skArc(sketch, "E675", {"start": v(-167.75, 42.35) * mm, "mid": v(-166.64, 42.57) * mm, "end": v(-165.53, 42.8) * mm});
            skArc(sketch, "E676", {"start": v(-165.53, 42.8) * mm, "mid": v(-164.57, 43) * mm, "end": v(-163.61, 43.2) * mm});
            skArc(sketch, "E677", {"start": v(-163.61, 43.2) * mm, "mid": v(-163.05, 43.32) * mm, "end": v(-162.5, 43.44) * mm});
            skArc(sketch, "E678", {"start": v(-162.5, 43.44) * mm, "mid": v(-160.47, 43.77) * mm, "end": v(-158.42, 43.84) * mm});
            skArc(sketch, "E679", {"start": v(-158.42, 43.84) * mm, "mid": v(-154.67, 43.66) * mm, "end": v(-150.92, 43.4) * mm});
            skArc(sketch, "E680", {"start": v(-150.92, 43.4) * mm, "mid": v(-147.15, 43.04) * mm, "end": v(-143.4, 42.58) * mm});
            skArc(sketch, "E681", {"start": v(-143.4, 42.58) * mm, "mid": v(-141.07, 42.14) * mm, "end": v(-138.8, 41.48) * mm});
            skArc(sketch, "E682", {"start": v(409.72, 42.75) * mm, "mid": v(409.53, 42.26) * mm, "end": v(409.33, 41.78) * mm});
            skArc(sketch, "E683", {"start": v(409.33, 41.78) * mm, "mid": v(407.35, 36.9) * mm, "end": v(405.36, 32.03) * mm});
            skArc(sketch, "E684", {"start": v(405.36, 32.03) * mm, "mid": v(403.1, 26.48) * mm, "end": v(400.83, 20.93) * mm});
            skArc(sketch, "E685", {"start": v(400.83, 20.93) * mm, "mid": v(398.2, 14.47) * mm, "end": v(395.55, 8) * mm});
            skArc(sketch, "E686", {"start": v(395.55, 8) * mm, "mid": v(392.76, 1.18) * mm, "end": v(389.98, -5.65) * mm});
            skArc(sketch, "E687", {"start": v(389.98, -5.65) * mm, "mid": v(387.26, -12.3) * mm, "end": v(384.54, -18.96) * mm});
            skArc(sketch, "E688", {"start": v(384.54, -18.96) * mm, "mid": v(382.21, -24.67) * mm, "end": v(379.88, -30.38) * mm});
            skArc(sketch, "E689", {"start": v(379.88, -30.38) * mm, "mid": v(378.6, -33.55) * mm, "end": v(377.3, -36.73) * mm});
            skArc(sketch, "E690", {"start": v(377.3, -36.73) * mm, "mid": v(375.84, -40.27) * mm, "end": v(374.36, -43.8) * mm});
            skArc(sketch, "E691", {"start": v(374.36, -43.8) * mm, "mid": v(373.69, -45.17) * mm, "end": v(372.89, -46.49) * mm});
            skArc(sketch, "E692", {"start": v(372.89, -46.49) * mm, "mid": v(372.24, -47.25) * mm, "end": v(371.42, -47.83) * mm});
            skArc(sketch, "E693", {"start": v(371.42, -47.83) * mm, "mid": v(370.39, -48.3) * mm, "end": v(369.3, -48.6) * mm});
            skArc(sketch, "E694", {"start": v(369.3, -48.6) * mm, "mid": v(367.54, -48.85) * mm, "end": v(365.77, -48.91) * mm});
            skArc(sketch, "E695", {"start": v(365.77, -48.91) * mm, "mid": v(363.66, -48.83) * mm, "end": v(361.56, -48.62) * mm});
            skArc(sketch, "E696", {"start": v(361.56, -48.62) * mm, "mid": v(359.41, -48.28) * mm, "end": v(357.29, -47.82) * mm});
            skArc(sketch, "E697", {"start": v(357.29, -47.82) * mm, "mid": v(355.4, -47.27) * mm, "end": v(353.54, -46.58) * mm});
            skArc(sketch, "E698", {"start": v(353.54, -46.58) * mm, "mid": v(351.9, -45.74) * mm, "end": v(350.42, -44.64) * mm});
            skArc(sketch, "E699", {"start": v(350.42, -44.64) * mm, "mid": v(349.09, -43.3) * mm, "end": v(347.98, -41.78) * mm});
            skArc(sketch, "E700", {"start": v(347.98, -41.78) * mm, "mid": v(347.13, -40.14) * mm, "end": v(346.54, -38.4) * mm});
            skArc(sketch, "E701", {"start": v(346.54, -38.4) * mm, "mid": v(346.28, -36.68) * mm, "end": v(346.33, -34.94) * mm});
            skArc(sketch, "E702", {"start": v(346.33, -34.94) * mm, "mid": v(346.68, -33.07) * mm, "end": v(347.27, -31.26) * mm});
            skArc(sketch, "E703", {"start": v(347.27, -31.26) * mm, "mid": v(354.24, -13.82) * mm, "end": v(361.22, 3.61) * mm});
            skArc(sketch, "E704", {"start": v(361.22, 3.61) * mm, "mid": v(368.02, 20.53) * mm, "end": v(374.84, 37.45) * mm});
            skArc(sketch, "E705", {"start": v(374.84, 37.45) * mm, "mid": v(376.16, 40.4) * mm, "end": v(377.68, 43.25) * mm});
            skArc(sketch, "E706", {"start": v(377.68, 43.25) * mm, "mid": v(377.9, 43.46) * mm, "end": v(378.18, 43.55) * mm});
            skArc(sketch, "E707", {"start": v(378.18, 43.55) * mm, "mid": v(380.44, 43.67) * mm, "end": v(382.7, 43.78) * mm});
            skArc(sketch, "E708", {"start": v(382.7, 43.78) * mm, "mid": v(385.34, 43.88) * mm, "end": v(387.98, 43.95) * mm});
            skArc(sketch, "E709", {"start": v(387.98, 43.95) * mm, "mid": v(391.07, 43.99) * mm, "end": v(394.17, 44) * mm});
            skArc(sketch, "E710", {"start": v(394.17, 44) * mm, "mid": v(398.22, 43.99) * mm, "end": v(402.27, 43.95) * mm});
            skArc(sketch, "E711", {"start": v(402.27, 43.95) * mm, "mid": v(404.51, 43.88) * mm, "end": v(406.75, 43.74) * mm});
            skArc(sketch, "E712", {"start": v(406.75, 43.74) * mm, "mid": v(408.06, 43.6) * mm, "end": v(409.37, 43.4) * mm});
            skArc(sketch, "E713", {"start": v(409.37, 43.4) * mm, "mid": v(409.7, 43.16) * mm, "end": v(409.72, 42.75) * mm});
            skArc(sketch, "E714", {"start": v(492.73, 42.75) * mm, "mid": v(490.55, 37.37) * mm, "end": v(488.2, 32.06) * mm});
            skArc(sketch, "E715", {"start": v(488.2, 32.06) * mm, "mid": v(486.53, 28.91) * mm, "end": v(484.5, 25.98) * mm});
            skArc(sketch, "E716", {"start": v(484.5, 25.98) * mm, "mid": v(481.73, 22.68) * mm, "end": v(478.73, 19.56) * mm});
            skArc(sketch, "E717", {"start": v(478.73, 19.56) * mm, "mid": v(470.5, 11.64) * mm, "end": v(462.23, 3.76) * mm});
            skArc(sketch, "E718", {"start": v(462.23, 3.76) * mm, "mid": v(457.55, -0.67) * mm, "end": v(452.86, -5.1) * mm});
            skArc(sketch, "E719", {"start": v(452.86, -5.1) * mm, "mid": v(448.52, -9.19) * mm, "end": v(444.17, -13.28) * mm});
            skArc(sketch, "E720", {"start": v(444.17, -13.28) * mm, "mid": v(440.51, -16.71) * mm, "end": v(436.85, -20.14) * mm});
            skArc(sketch, "E721", {"start": v(436.85, -20.14) * mm, "mid": v(435.3, -21.58) * mm, "end": v(433.75, -23) * mm});
            skLineSegment(sketch, "E722", {"start": v(433.75, -23) * mm, "end": v(428.77, -27.5) * mm});
            skLineSegment(sketch, "E723", {"start": v(428.77, -27.5) * mm, "end": v(447.38, -27.19) * mm});
            skArc(sketch, "E724", {"start": v(447.38, -27.19) * mm, "mid": v(450.95, -27.14) * mm, "end": v(454.52, -27.1) * mm});
            skArc(sketch, "E725", {"start": v(454.52, -27.1) * mm, "mid": v(457.53, -27.1) * mm, "end": v(460.53, -27.1) * mm});
            skArc(sketch, "E726", {"start": v(460.53, -27.1) * mm, "mid": v(463.17, -27.13) * mm, "end": v(465.81, -27.16) * mm});
            skArc(sketch, "E727", {"start": v(465.81, -27.16) * mm, "mid": v(465.95, -27.21) * mm, "end": v(466, -27.34) * mm});
            skArc(sketch, "E728", {"start": v(466, -27.34) * mm, "mid": v(465.98, -27.52) * mm, "end": v(465.93, -27.7) * mm});
            skArc(sketch, "E729", {"start": v(465.93, -27.7) * mm, "mid": v(465.32, -29.2) * mm, "end": v(464.7, -30.71) * mm});
            skArc(sketch, "E730", {"start": v(464.7, -30.71) * mm, "mid": v(464, -32.44) * mm, "end": v(463.27, -34.16) * mm});
            skArc(sketch, "E731", {"start": v(463.27, -34.16) * mm, "mid": v(462.43, -36.16) * mm, "end": v(461.58, -38.16) * mm});
            skLineSegment(sketch, "E732", {"start": v(461.58, -38.16) * mm, "end": v(457.15, -48.5) * mm});
            skLineSegment(sketch, "E733", {"start": v(457.15, -48.5) * mm, "end": v(418.46, -48.76) * mm});
            skArc(sketch, "E734", {"start": v(418.46, -48.76) * mm, "mid": v(408.43, -48.82) * mm, "end": v(398.39, -48.85) * mm});
            skArc(sketch, "E735", {"start": v(398.39, -48.85) * mm, "mid": v(393.02, -48.82) * mm, "end": v(387.66, -48.72) * mm});
            skArc(sketch, "E736", {"start": v(387.66, -48.72) * mm, "mid": v(384.2, -48.6) * mm, "end": v(380.73, -48.46) * mm});
            skArc(sketch, "E737", {"start": v(380.73, -48.46) * mm, "mid": v(380.32, -48.23) * mm, "end": v(380.28, -47.76) * mm});
            skArc(sketch, "E738", {"start": v(380.28, -47.76) * mm, "mid": v(382.42, -42.62) * mm, "end": v(384.74, -37.55) * mm});
            skArc(sketch, "E739", {"start": v(384.74, -37.55) * mm, "mid": v(386.46, -34.46) * mm, "end": v(388.56, -31.62) * mm});
            skArc(sketch, "E740", {"start": v(388.56, -31.62) * mm, "mid": v(391.6, -28.2) * mm, "end": v(394.85, -24.97) * mm});
            skArc(sketch, "E741", {"start": v(394.85, -24.97) * mm, "mid": v(405.47, -15) * mm, "end": v(416.13, -5.05) * mm});
            skLineSegment(sketch, "E742", {"start": v(416.13, -5.05) * mm, "end": v(445.76, 22.5) * mm});
            skLineSegment(sketch, "E743", {"start": v(445.76, 22.5) * mm, "end": v(427.78, 22.77) * mm});
            skArc(sketch, "E744", {"start": v(427.78, 22.77) * mm, "mid": v(423.31, 22.85) * mm, "end": v(418.84, 22.96) * mm});
            skArc(sketch, "E745", {"start": v(418.84, 22.96) * mm, "mid": v(416.3, 23.07) * mm, "end": v(413.75, 23.25) * mm});
            skArc(sketch, "E746", {"start": v(413.75, 23.25) * mm, "mid": v(412.2, 23.41) * mm, "end": v(410.65, 23.63) * mm});
            skArc(sketch, "E747", {"start": v(410.65, 23.63) * mm, "mid": v(410.32, 23.87) * mm, "end": v(410.3, 24.27) * mm});
            skArc(sketch, "E748", {"start": v(410.3, 24.27) * mm, "mid": v(410.46, 24.7) * mm, "end": v(410.64, 25.1) * mm});
            skArc(sketch, "E749", {"start": v(410.64, 25.1) * mm, "mid": v(411.26, 26.48) * mm, "end": v(411.88, 27.86) * mm});
            skArc(sketch, "E750", {"start": v(411.88, 27.86) * mm, "mid": v(412.62, 29.49) * mm, "end": v(413.37, 31.12) * mm});
            skArc(sketch, "E751", {"start": v(413.37, 31.12) * mm, "mid": v(414.2, 32.93) * mm, "end": v(415.03, 34.75) * mm});
            skLineSegment(sketch, "E752", {"start": v(415.03, 34.75) * mm, "end": v(419.28, 44) * mm});
            skLineSegment(sketch, "E753", {"start": v(419.28, 44) * mm, "end": v(456.25, 44) * mm});
            skArc(sketch, "E754", {"start": v(456.25, 44) * mm, "mid": v(465.75, 43.99) * mm, "end": v(475.25, 43.95) * mm});
            skArc(sketch, "E755", {"start": v(475.25, 43.95) * mm, "mid": v(480.41, 43.88) * mm, "end": v(485.57, 43.74) * mm});
            skArc(sketch, "E756", {"start": v(485.57, 43.74) * mm, "mid": v(488.93, 43.61) * mm, "end": v(492.28, 43.44) * mm});
            skArc(sketch, "E757", {"start": v(492.28, 43.44) * mm, "mid": v(492.68, 43.21) * mm, "end": v(492.73, 42.75) * mm});
            skArc(sketch, "E758", {"start": v(156.75, 38) * mm, "mid": v(157.01, 37.04) * mm, "end": v(157.24, 36.08) * mm});
            skArc(sketch, "E759", {"start": v(157.24, 36.08) * mm, "mid": v(157.43, 35.07) * mm, "end": v(157.6, 34.05) * mm});
            skArc(sketch, "E760", {"start": v(157.6, 34.05) * mm, "mid": v(157.7, 33.13) * mm, "end": v(157.78, 32.2) * mm});
            skArc(sketch, "E761", {"start": v(157.78, 32.2) * mm, "mid": v(157.8, 31.54) * mm, "end": v(157.74, 30.89) * mm});
            skArc(sketch, "E762", {"start": v(157.74, 30.89) * mm, "mid": v(157.69, 30.19) * mm, "end": v(157.73, 29.48) * mm});
            skArc(sketch, "E763", {"start": v(157.73, 29.48) * mm, "mid": v(157.9, 29.2) * mm, "end": v(158.22, 29.15) * mm});
            skArc(sketch, "E764", {"start": v(158.22, 29.15) * mm, "mid": v(158.84, 29.38) * mm, "end": v(159.41, 29.7) * mm});
            skArc(sketch, "E765", {"start": v(159.41, 29.7) * mm, "mid": v(161.51, 31.11) * mm, "end": v(163.6, 32.53) * mm});
            skArc(sketch, "E766", {"start": v(163.6, 32.53) * mm, "mid": v(167.73, 35.12) * mm, "end": v(172.06, 37.36) * mm});
            skArc(sketch, "E767", {"start": v(172.06, 37.36) * mm, "mid": v(176.57, 39.24) * mm, "end": v(181.22, 40.75) * mm});
            skArc(sketch, "E768", {"start": v(181.22, 40.75) * mm, "mid": v(185.94, 41.86) * mm, "end": v(190.74, 42.58) * mm});
            skArc(sketch, "E769", {"start": v(190.74, 42.58) * mm, "mid": v(195.5, 42.9) * mm, "end": v(200.26, 42.8) * mm});
            skArc(sketch, "E770", {"start": v(200.26, 42.8) * mm, "mid": v(204.52, 42.3) * mm, "end": v(208.7, 41.42) * mm});
            skArc(sketch, "E771", {"start": v(208.7, 41.42) * mm, "mid": v(211.46, 40.27) * mm, "end": v(213.8, 38.42) * mm});
            skArc(sketch, "E772", {"start": v(213.8, 38.42) * mm, "mid": v(215.45, 36.09) * mm, "end": v(216.36, 33.38) * mm});
            skArc(sketch, "E773", {"start": v(216.36, 33.38) * mm, "mid": v(216.8, 29.49) * mm, "end": v(216.78, 25.57) * mm});
            skArc(sketch, "E774", {"start": v(216.78, 25.57) * mm, "mid": v(216.5, 22.99) * mm, "end": v(216, 20.44) * mm});
            skArc(sketch, "E775", {"start": v(216, 20.44) * mm, "mid": v(215.2, 17.46) * mm, "end": v(214.23, 14.52) * mm});
            skArc(sketch, "E776", {"start": v(214.23, 14.52) * mm, "mid": v(212.55, 9.98) * mm, "end": v(210.76, 5.48) * mm});
            skArc(sketch, "E777", {"start": v(210.76, 5.48) * mm, "mid": v(206.96, -3.65) * mm, "end": v(203.14, -12.76) * mm});
            skArc(sketch, "E778", {"start": v(203.14, -12.76) * mm, "mid": v(200.57, -18.84) * mm, "end": v(198, -24.92) * mm});
            skArc(sketch, "E779", {"start": v(198, -24.92) * mm, "mid": v(195.75, -30.24) * mm, "end": v(193.49, -35.57) * mm});
            skArc(sketch, "E780", {"start": v(193.49, -35.57) * mm, "mid": v(191.56, -40.12) * mm, "end": v(189.62, -44.67) * mm});
            skArc(sketch, "E781", {"start": v(189.62, -44.67) * mm, "mid": v(189.22, -45.6) * mm, "end": v(188.81, -46.5) * mm});
            skLineSegment(sketch, "E782", {"start": v(188.81, -46.5) * mm, "end": v(187.68, -49) * mm});
            skLineSegment(sketch, "E783", {"start": v(187.68, -49) * mm, "end": v(171.84, -49) * mm});
            skArc(sketch, "E784", {"start": v(171.84, -49) * mm, "mid": v(168.8, -48.98) * mm, "end": v(165.77, -48.94) * mm});
            skArc(sketch, "E785", {"start": v(165.77, -48.94) * mm, "mid": v(163.2, -48.86) * mm, "end": v(160.65, -48.74) * mm});
            skArc(sketch, "E786", {"start": v(160.65, -48.74) * mm, "mid": v(158.5, -48.6) * mm, "end": v(156.34, -48.46) * mm});
            skArc(sketch, "E787", {"start": v(156.34, -48.46) * mm, "mid": v(156.1, -48.35) * mm, "end": v(156, -48.1) * mm});
            skArc(sketch, "E788", {"start": v(156, -48.1) * mm, "mid": v(156.03, -47.75) * mm, "end": v(156.13, -47.42) * mm});
            skArc(sketch, "E789", {"start": v(156.13, -47.42) * mm, "mid": v(157.89, -43.13) * mm, "end": v(159.64, -38.84) * mm});
            skArc(sketch, "E790", {"start": v(159.64, -38.84) * mm, "mid": v(161.63, -34) * mm, "end": v(163.64, -29.17) * mm});
            skArc(sketch, "E791", {"start": v(163.64, -29.17) * mm, "mid": v(166.01, -23.5) * mm, "end": v(168.4, -17.85) * mm});
            skArc(sketch, "E792", {"start": v(168.4, -17.85) * mm, "mid": v(170.8, -12.11) * mm, "end": v(173.2, -6.37) * mm});
            skArc(sketch, "E793", {"start": v(173.2, -6.37) * mm, "mid": v(175.29, -1.27) * mm, "end": v(177.35, 3.84) * mm});
            skArc(sketch, "E794", {"start": v(177.35, 3.84) * mm, "mid": v(179.08, 8.18) * mm, "end": v(180.8, 12.51) * mm});
            skArc(sketch, "E795", {"start": v(180.8, 12.51) * mm, "mid": v(181.19, 13.64) * mm, "end": v(181.48, 14.8) * mm});
            skArc(sketch, "E796", {"start": v(181.48, 14.8) * mm, "mid": v(181.42, 17.23) * mm, "end": v(180.27, 19.38) * mm});
            skArc(sketch, "E797", {"start": v(180.27, 19.38) * mm, "mid": v(178.34, 20.66) * mm, "end": v(176.02, 20.77) * mm});
            skArc(sketch, "E798", {"start": v(176.02, 20.77) * mm, "mid": v(172.2, 19.49) * mm, "end": v(168.72, 17.41) * mm});
            skArc(sketch, "E799", {"start": v(168.72, 17.41) * mm, "mid": v(164.64, 14.02) * mm, "end": v(160.91, 10.25) * mm});
            skArc(sketch, "E800", {"start": v(160.91, 10.25) * mm, "mid": v(159.1, 8.06) * mm, "end": v(157.47, 5.73) * mm});
            skArc(sketch, "E801", {"start": v(157.47, 5.73) * mm, "mid": v(155.81, 2.97) * mm, "end": v(154.32, 0.13) * mm});
            skArc(sketch, "E802", {"start": v(154.32, 0.13) * mm, "mid": v(152.13, -4.48) * mm, "end": v(150.05, -9.14) * mm});
            skArc(sketch, "E803", {"start": v(150.05, -9.14) * mm, "mid": v(145.59, -19.56) * mm, "end": v(141.15, -30) * mm});
            skLineSegment(sketch, "E804", {"start": v(141.15, -30) * mm, "end": v(133.32, -48.5) * mm});
            skLineSegment(sketch, "E805", {"start": v(133.32, -48.5) * mm, "end": v(117.05, -48.78) * mm});
            skArc(sketch, "E806", {"start": v(117.05, -48.78) * mm, "mid": v(112.85, -48.83) * mm, "end": v(108.66, -48.87) * mm});
            skArc(sketch, "E807", {"start": v(108.66, -48.87) * mm, "mid": v(106.42, -48.84) * mm, "end": v(104.18, -48.74) * mm});
            skArc(sketch, "E808", {"start": v(104.18, -48.74) * mm, "mid": v(102.9, -48.62) * mm, "end": v(101.64, -48.43) * mm});
            skArc(sketch, "E809", {"start": v(101.64, -48.43) * mm, "mid": v(101.3, -48.19) * mm, "end": v(101.28, -47.78) * mm});
            skArc(sketch, "E810", {"start": v(101.28, -47.78) * mm, "mid": v(101.48, -47.29) * mm, "end": v(101.68, -46.8) * mm});
            skArc(sketch, "E811", {"start": v(101.68, -46.8) * mm, "mid": v(103.28, -43.02) * mm, "end": v(104.88, -39.24) * mm});
            skArc(sketch, "E812", {"start": v(104.88, -39.24) * mm, "mid": v(106.71, -34.9) * mm, "end": v(108.55, -30.56) * mm});
            skArc(sketch, "E813", {"start": v(108.55, -30.56) * mm, "mid": v(110.68, -25.53) * mm, "end": v(112.8, -20.5) * mm});
            skArc(sketch, "E814", {"start": v(112.8, -20.5) * mm, "mid": v(114.99, -15.33) * mm, "end": v(117.14, -10.14) * mm});
            skArc(sketch, "E815", {"start": v(117.14, -10.14) * mm, "mid": v(119.1, -5.34) * mm, "end": v(121.04, -0.52) * mm});
            skArc(sketch, "E816", {"start": v(121.04, -0.52) * mm, "mid": v(122.64, 3.52) * mm, "end": v(124.22, 7.58) * mm});
            skArc(sketch, "E817", {"start": v(124.22, 7.58) * mm, "mid": v(124.83, 9.28) * mm, "end": v(125.36, 11) * mm});
            skArc(sketch, "E818", {"start": v(125.36, 11) * mm, "mid": v(126.12, 13.98) * mm, "end": v(126.76, 17) * mm});
            skArc(sketch, "E819", {"start": v(126.76, 17) * mm, "mid": v(127.23, 19.83) * mm, "end": v(127.55, 22.7) * mm});
            skArc(sketch, "E820", {"start": v(127.55, 22.7) * mm, "mid": v(127.7, 25.2) * mm, "end": v(127.7, 27.7) * mm});
            skArc(sketch, "E821", {"start": v(127.7, 27.7) * mm, "mid": v(127.52, 29.63) * mm, "end": v(127.12, 31.52) * mm});
            skArc(sketch, "E822", {"start": v(127.12, 31.52) * mm, "mid": v(126.92, 32.28) * mm, "end": v(126.74, 33.03) * mm});
            skArc(sketch, "E823", {"start": v(126.74, 33.03) * mm, "mid": v(126.6, 33.7) * mm, "end": v(126.49, 34.37) * mm});
            skArc(sketch, "E824", {"start": v(126.49, 34.37) * mm, "mid": v(126.4, 34.92) * mm, "end": v(126.35, 35.47) * mm});
            skArc(sketch, "E825", {"start": v(126.35, 35.47) * mm, "mid": v(126.37, 35.65) * mm, "end": v(126.46, 35.8) * mm});
            skArc(sketch, "E826", {"start": v(126.46, 35.8) * mm, "mid": v(127.03, 36.23) * mm, "end": v(127.7, 36.5) * mm});
            skArc(sketch, "E827", {"start": v(127.7, 36.5) * mm, "mid": v(133.8, 38.04) * mm, "end": v(139.93, 39.57) * mm});
            skArc(sketch, "E828", {"start": v(139.93, 39.57) * mm, "mid": v(145.93, 41.07) * mm, "end": v(151.94, 42.54) * mm});
            skArc(sketch, "E829", {"start": v(151.94, 42.54) * mm, "mid": v(152.94, 42.7) * mm, "end": v(153.96, 42.66) * mm});
            skArc(sketch, "E830", {"start": v(153.96, 42.66) * mm, "mid": v(154.32, 42.55) * mm, "end": v(154.6, 42.31) * mm});
            skArc(sketch, "E831", {"start": v(154.6, 42.31) * mm, "mid": v(155.01, 41.78) * mm, "end": v(155.38, 41.22) * mm});
            skArc(sketch, "E832", {"start": v(155.38, 41.22) * mm, "mid": v(155.78, 40.49) * mm, "end": v(156.13, 39.73) * mm});
            skArc(sketch, "E833", {"start": v(156.13, 39.73) * mm, "mid": v(156.47, 38.87) * mm, "end": v(156.75, 38) * mm});
            skArc(sketch, "E834", {"start": v(235.63, -19.36) * mm, "mid": v(237.43, -22.58) * mm, "end": v(237.8, -26.25) * mm});
            skArc(sketch, "E835", {"start": v(237.8, -26.25) * mm, "mid": v(236.86, -30.75) * mm, "end": v(234.98, -34.95) * mm});
            skArc(sketch, "E836", {"start": v(234.98, -34.95) * mm, "mid": v(231.91, -39.26) * mm, "end": v(228.13, -42.94) * mm});
            skArc(sketch, "E837", {"start": v(228.13, -42.94) * mm, "mid": v(223.86, -45.75) * mm, "end": v(219.12, -47.65) * mm});
            skArc(sketch, "E838", {"start": v(219.12, -47.65) * mm, "mid": v(216.95, -48.19) * mm, "end": v(214.74, -48.53) * mm});
            skArc(sketch, "E839", {"start": v(214.74, -48.53) * mm, "mid": v(212.5, -48.7) * mm, "end": v(210.24, -48.67) * mm});
            skArc(sketch, "E840", {"start": v(210.24, -48.67) * mm, "mid": v(208.19, -48.48) * mm, "end": v(206.16, -48.1) * mm});
            skArc(sketch, "E841", {"start": v(206.16, -48.1) * mm, "mid": v(204.58, -47.59) * mm, "end": v(203.1, -46.83) * mm});
            skArc(sketch, "E842", {"start": v(203.1, -46.83) * mm, "mid": v(201.16, -45.13) * mm, "end": v(199.88, -42.9) * mm});
            skArc(sketch, "E843", {"start": v(199.88, -42.9) * mm, "mid": v(199.2, -40.13) * mm, "end": v(199.2, -37.28) * mm});
            skArc(sketch, "E844", {"start": v(199.2, -37.28) * mm, "mid": v(199.94, -33.95) * mm, "end": v(201.28, -30.82) * mm});
            skArc(sketch, "E845", {"start": v(201.28, -30.82) * mm, "mid": v(203.33, -27.6) * mm, "end": v(205.8, -24.67) * mm});
            skArc(sketch, "E846", {"start": v(205.8, -24.67) * mm, "mid": v(208.08, -22.49) * mm, "end": v(210.54, -20.5) * mm});
            skArc(sketch, "E847", {"start": v(210.54, -20.5) * mm, "mid": v(212.8, -19.04) * mm, "end": v(215.24, -17.9) * mm});
            skArc(sketch, "E848", {"start": v(215.24, -17.9) * mm, "mid": v(217.82, -17.06) * mm, "end": v(220.48, -16.57) * mm});
            skArc(sketch, "E849", {"start": v(220.48, -16.57) * mm, "mid": v(223.68, -16.33) * mm, "end": v(226.88, -16.34) * mm});
            skArc(sketch, "E850", {"start": v(226.88, -16.34) * mm, "mid": v(228.69, -16.44) * mm, "end": v(230.5, -16.6) * mm});
            skArc(sketch, "E851", {"start": v(230.5, -16.6) * mm, "mid": v(231.54, -16.76) * mm, "end": v(232.57, -17.04) * mm});
            skArc(sketch, "E852", {"start": v(232.57, -17.04) * mm, "mid": v(233.37, -17.4) * mm, "end": v(234.1, -17.88) * mm});
            skArc(sketch, "E853", {"start": v(234.1, -17.88) * mm, "mid": v(234.9, -18.59) * mm, "end": v(235.63, -19.36) * mm});
            skArc(sketch, "E854", {"start": v(313.3, 51.21) * mm, "mid": v(312.65, 50.65) * mm, "end": v(312.19, 49.92) * mm});
            skArc(sketch, "E855", {"start": v(312.19, 49.92) * mm, "mid": v(309.21, 43.32) * mm, "end": v(306.25, 36.7) * mm});
            skArc(sketch, "E856", {"start": v(306.25, 36.7) * mm, "mid": v(303.35, 30.2) * mm, "end": v(300.47, 23.68) * mm});
            skArc(sketch, "E857", {"start": v(300.47, 23.68) * mm, "mid": v(300.12, 22.58) * mm, "end": v(300, 21.42) * mm});
            skArc(sketch, "E858", {"start": v(300, 21.42) * mm, "mid": v(300.24, 20.89) * mm, "end": v(300.8, 20.7) * mm});
            skArc(sketch, "E859", {"start": v(300.8, 20.7) * mm, "mid": v(304.04, 21) * mm, "end": v(307.28, 21.35) * mm});
            skArc(sketch, "E860", {"start": v(307.28, 21.35) * mm, "mid": v(310.46, 21.78) * mm, "end": v(313.62, 22.3) * mm});
            skArc(sketch, "E861", {"start": v(313.62, 22.3) * mm, "mid": v(315.65, 22.78) * mm, "end": v(317.62, 23.48) * mm});
            skArc(sketch, "E862", {"start": v(317.62, 23.48) * mm, "mid": v(319.53, 24.4) * mm, "end": v(321.35, 25.48) * mm});
            skArc(sketch, "E863", {"start": v(321.35, 25.48) * mm, "mid": v(323.03, 26.71) * mm, "end": v(324.57, 28.1) * mm});
            skArc(sketch, "E864", {"start": v(324.57, 28.1) * mm, "mid": v(326.02, 29.7) * mm, "end": v(327.3, 31.43) * mm});
            skArc(sketch, "E865", {"start": v(327.3, 31.43) * mm, "mid": v(328.54, 33.42) * mm, "end": v(329.62, 35.5) * mm});
            skArc(sketch, "E866", {"start": v(329.62, 35.5) * mm, "mid": v(330.47, 37.47) * mm, "end": v(331.18, 39.49) * mm});
            skArc(sketch, "E867", {"start": v(331.18, 39.49) * mm, "mid": v(331.63, 41.25) * mm, "end": v(331.88, 43.05) * mm});
            skArc(sketch, "E868", {"start": v(331.88, 43.05) * mm, "mid": v(331.9, 44.56) * mm, "end": v(331.72, 46.06) * mm});
            skArc(sketch, "E869", {"start": v(331.72, 46.06) * mm, "mid": v(331.33, 47.3) * mm, "end": v(330.7, 48.4) * mm});
            skArc(sketch, "E870", {"start": v(330.7, 48.4) * mm, "mid": v(329.55, 49.53) * mm, "end": v(328.1, 50.22) * mm});
            skArc(sketch, "E871", {"start": v(328.1, 50.22) * mm, "mid": v(325.26, 50.96) * mm, "end": v(322.37, 51.51) * mm});
            skArc(sketch, "E872", {"start": v(322.37, 51.51) * mm, "mid": v(319.45, 51.9) * mm, "end": v(316.5, 52.08) * mm});
            skArc(sketch, "E873", {"start": v(316.5, 52.08) * mm, "mid": v(314.84, 51.89) * mm, "end": v(313.3, 51.21) * mm});
            skArc(sketch, "E874", {"start": v(286, -10.16) * mm, "mid": v(284.94, -12.64) * mm, "end": v(283.87, -15.13) * mm});
            skArc(sketch, "E875", {"start": v(283.87, -15.13) * mm, "mid": v(282.86, -17.5) * mm, "end": v(281.84, -19.87) * mm});
            skArc(sketch, "E876", {"start": v(281.84, -19.87) * mm, "mid": v(280.98, -21.88) * mm, "end": v(280.13, -23.89) * mm});
            skArc(sketch, "E877", {"start": v(280.13, -23.89) * mm, "mid": v(279.7, -24.89) * mm, "end": v(279.28, -25.9) * mm});
            skLineSegment(sketch, "E878", {"start": v(279.28, -25.9) * mm, "end": v(277.85, -29.29) * mm});
            skLineSegment(sketch, "E879", {"start": v(277.85, -29.29) * mm, "end": v(286.68, -28.76) * mm});
            skArc(sketch, "E880", {"start": v(286.68, -28.76) * mm, "mid": v(288.52, -28.62) * mm, "end": v(290.37, -28.43) * mm});
            skArc(sketch, "E881", {"start": v(290.37, -28.43) * mm, "mid": v(292.27, -28.18) * mm, "end": v(294.16, -27.88) * mm});
            skArc(sketch, "E882", {"start": v(294.16, -27.88) * mm, "mid": v(295.85, -27.57) * mm, "end": v(297.53, -27.2) * mm});
            skArc(sketch, "E883", {"start": v(297.53, -27.2) * mm, "mid": v(298.66, -26.9) * mm, "end": v(299.77, -26.5) * mm});
            skArc(sketch, "E884", {"start": v(299.77, -26.5) * mm, "mid": v(302.52, -25.1) * mm, "end": v(305, -23.26) * mm});
            skArc(sketch, "E885", {"start": v(305, -23.26) * mm, "mid": v(307.47, -20.79) * mm, "end": v(309.64, -18.04) * mm});
            skArc(sketch, "E886", {"start": v(309.64, -18.04) * mm, "mid": v(311.45, -15.1) * mm, "end": v(312.9, -11.97) * mm});
            skArc(sketch, "E887", {"start": v(312.9, -11.97) * mm, "mid": v(313.72, -9.13) * mm, "end": v(314, -6.19) * mm});
            skArc(sketch, "E888", {"start": v(314, -6.19) * mm, "mid": v(313.96, -5.69) * mm, "end": v(313.83, -5.2) * mm});
            skArc(sketch, "E889", {"start": v(313.83, -5.2) * mm, "mid": v(313.58, -4.54) * mm, "end": v(313.3, -3.9) * mm});
            skArc(sketch, "E890", {"start": v(313.3, -3.9) * mm, "mid": v(312.92, -3.2) * mm, "end": v(312.51, -2.53) * mm});
            skArc(sketch, "E891", {"start": v(312.51, -2.53) * mm, "mid": v(312.07, -1.9) * mm, "end": v(311.59, -1.3) * mm});
            skArc(sketch, "E892", {"start": v(311.59, -1.3) * mm, "mid": v(310.78, -0.46) * mm, "end": v(309.9, 0.29) * mm});
            skArc(sketch, "E893", {"start": v(309.9, 0.29) * mm, "mid": v(309.09, 0.8) * mm, "end": v(308.2, 1.13) * mm});
            skArc(sketch, "E894", {"start": v(308.2, 1.13) * mm, "mid": v(306.95, 1.41) * mm, "end": v(305.67, 1.56) * mm});
            skArc(sketch, "E895", {"start": v(305.67, 1.56) * mm, "mid": v(302.96, 1.72) * mm, "end": v(300.24, 1.84) * mm});
            skLineSegment(sketch, "E896", {"start": v(300.24, 1.84) * mm, "end": v(291.31, 2.19) * mm});
            skLineSegment(sketch, "E897", {"start": v(291.31, 2.19) * mm, "end": v(286, -10.16) * mm});
            skArc(sketch, "E898", {"start": v(66.55, 18.94) * mm, "mid": v(63.5, 15.67) * mm, "end": v(60.94, 12) * mm});
            skArc(sketch, "E899", {"start": v(60.94, 12) * mm, "mid": v(57.84, 6.42) * mm, "end": v(55.04, 0.68) * mm});
            skArc(sketch, "E900", {"start": v(55.04, 0.68) * mm, "mid": v(52.55, -5.15) * mm, "end": v(50.37, -11.1) * mm});
            skArc(sketch, "E901", {"start": v(50.37, -11.1) * mm, "mid": v(49.35, -15.22) * mm, "end": v(49, -19.45) * mm});
            skArc(sketch, "E902", {"start": v(49, -19.45) * mm, "mid": v(49.1, -20.64) * mm, "end": v(49.37, -21.81) * mm});
            skArc(sketch, "E903", {"start": v(49.37, -21.81) * mm, "mid": v(49.82, -22.85) * mm, "end": v(50.46, -23.8) * mm});
            skArc(sketch, "E904", {"start": v(50.46, -23.8) * mm, "mid": v(51.28, -24.65) * mm, "end": v(52.24, -25.34) * mm});
            skArc(sketch, "E905", {"start": v(52.24, -25.34) * mm, "mid": v(53.43, -25.96) * mm, "end": v(54.68, -26.43) * mm});
            skArc(sketch, "E906", {"start": v(54.68, -26.43) * mm, "mid": v(55.8, -26.62) * mm, "end": v(56.93, -26.54) * mm});
            skArc(sketch, "E907", {"start": v(56.93, -26.54) * mm, "mid": v(58.62, -26.13) * mm, "end": v(60.28, -25.6) * mm});
            skArc(sketch, "E908", {"start": v(60.28, -25.6) * mm, "mid": v(62.02, -24.9) * mm, "end": v(63.7, -24.07) * mm});
            skArc(sketch, "E909", {"start": v(63.7, -24.07) * mm, "mid": v(65.08, -23.22) * mm, "end": v(66.36, -22.21) * mm});
            skArc(sketch, "E910", {"start": v(66.36, -22.21) * mm, "mid": v(69.72, -18.66) * mm, "end": v(72.41, -14.57) * mm});
            skArc(sketch, "E911", {"start": v(72.41, -14.57) * mm, "mid": v(75.66, -8.1) * mm, "end": v(78.52, -1.45) * mm});
            skArc(sketch, "E912", {"start": v(78.52, -1.45) * mm, "mid": v(80.96, 5.17) * mm, "end": v(83.06, 11.91) * mm});
            skArc(sketch, "E913", {"start": v(83.06, 11.91) * mm, "mid": v(83.5, 15.5) * mm, "end": v(82.78, 19.06) * mm});
            skArc(sketch, "E914", {"start": v(82.78, 19.06) * mm, "mid": v(82.33, 20.09) * mm, "end": v(81.75, 21.06) * mm});
            skArc(sketch, "E915", {"start": v(81.75, 21.06) * mm, "mid": v(81.17, 21.72) * mm, "end": v(80.45, 22.22) * mm});
            skArc(sketch, "E916", {"start": v(80.45, 22.22) * mm, "mid": v(79.5, 22.6) * mm, "end": v(78.49, 22.8) * mm});
            skArc(sketch, "E917", {"start": v(78.49, 22.8) * mm, "mid": v(76.86, 22.94) * mm, "end": v(75.23, 22.98) * mm});
            skArc(sketch, "E918", {"start": v(75.23, 22.98) * mm, "mid": v(74, 22.94) * mm, "end": v(72.8, 22.81) * mm});
            skArc(sketch, "E919", {"start": v(72.8, 22.81) * mm, "mid": v(71.84, 22.6) * mm, "end": v(70.93, 22.26) * mm});
            skArc(sketch, "E920", {"start": v(70.93, 22.26) * mm, "mid": v(69.97, 21.73) * mm, "end": v(69.07, 21.1) * mm});
            skArc(sketch, "E921", {"start": v(69.07, 21.1) * mm, "mid": v(67.8, 20.04) * mm, "end": v(66.55, 18.94) * mm});
            skArc(sketch, "E922", {"start": v(-512.55, 22.6) * mm, "mid": v(-514.02, 21.83) * mm, "end": v(-515.36, 20.86) * mm});
            skArc(sketch, "E923", {"start": v(-515.36, 20.86) * mm, "mid": v(-516.85, 19.51) * mm, "end": v(-518.22, 18.05) * mm});
            skArc(sketch, "E924", {"start": v(-518.22, 18.05) * mm, "mid": v(-519.68, 16.25) * mm, "end": v(-521, 14.35) * mm});
            skArc(sketch, "E925", {"start": v(-521, 14.35) * mm, "mid": v(-522.34, 12.15) * mm, "end": v(-523.56, 9.9) * mm});
            skArc(sketch, "E926", {"start": v(-523.56, 9.9) * mm, "mid": v(-524.65, 7.68) * mm, "end": v(-525.7, 5.45) * mm});
            skArc(sketch, "E927", {"start": v(-525.7, 5.45) * mm, "mid": v(-525.9, 4.68) * mm, "end": v(-525.82, 3.89) * mm});
            skArc(sketch, "E928", {"start": v(-525.82, 3.89) * mm, "mid": v(-525.46, 3.38) * mm, "end": v(-524.87, 3.2) * mm});
            skArc(sketch, "E929", {"start": v(-524.87, 3.2) * mm, "mid": v(-523.3, 3.32) * mm, "end": v(-521.75, 3.53) * mm});
            skArc(sketch, "E930", {"start": v(-521.75, 3.53) * mm, "mid": v(-518.42, 4.3) * mm, "end": v(-515.2, 5.44) * mm});
            skArc(sketch, "E931", {"start": v(-515.2, 5.44) * mm, "mid": v(-512.1, 6.96) * mm, "end": v(-509.22, 8.82) * mm});
            skArc(sketch, "E932", {"start": v(-509.22, 8.82) * mm, "mid": v(-506.81, 10.82) * mm, "end": v(-504.68, 13.1) * mm});
            skArc(sketch, "E933", {"start": v(-504.68, 13.1) * mm, "mid": v(-503.26, 15.27) * mm, "end": v(-502.36, 17.69) * mm});
            skArc(sketch, "E934", {"start": v(-502.36, 17.69) * mm, "mid": v(-502.23, 18.38) * mm, "end": v(-502.16, 19.08) * mm});
            skArc(sketch, "E935", {"start": v(-502.16, 19.08) * mm, "mid": v(-502.18, 19.63) * mm, "end": v(-502.32, 20.16) * mm});
            skArc(sketch, "E936", {"start": v(-502.32, 20.16) * mm, "mid": v(-502.55, 20.68) * mm, "end": v(-502.89, 21.14) * mm});
            skArc(sketch, "E937", {"start": v(-502.89, 21.14) * mm, "mid": v(-503.4, 21.68) * mm, "end": v(-503.96, 22.17) * mm});
            skArc(sketch, "E938", {"start": v(-503.96, 22.17) * mm, "mid": v(-504.89, 22.84) * mm, "end": v(-505.89, 23.4) * mm});
            skArc(sketch, "E939", {"start": v(-505.89, 23.4) * mm, "mid": v(-506.77, 23.73) * mm, "end": v(-507.7, 23.87) * mm});
            skArc(sketch, "E940", {"start": v(-507.7, 23.87) * mm, "mid": v(-508.73, 23.83) * mm, "end": v(-509.75, 23.62) * mm});
            skArc(sketch, "E941", {"start": v(-509.75, 23.62) * mm, "mid": v(-511.17, 23.15) * mm, "end": v(-512.55, 22.6) * mm});
            skArc(sketch, "E942", {"start": v(-319.47, 21.03) * mm, "mid": v(-321.17, 19.77) * mm, "end": v(-322.7, 18.32) * mm});
            skArc(sketch, "E943", {"start": v(-322.7, 18.32) * mm, "mid": v(-324.33, 16.48) * mm, "end": v(-325.8, 14.52) * mm});
            skArc(sketch, "E944", {"start": v(-325.8, 14.52) * mm, "mid": v(-327.28, 12.25) * mm, "end": v(-328.6, 9.89) * mm});
            skArc(sketch, "E945", {"start": v(-328.6, 9.89) * mm, "mid": v(-329.85, 7.3) * mm, "end": v(-330.95, 4.63) * mm});
            skArc(sketch, "E946", {"start": v(-330.95, 4.63) * mm, "mid": v(-331.18, 3.94) * mm, "end": v(-331.35, 3.24) * mm});
            skArc(sketch, "E947", {"start": v(-331.35, 3.24) * mm, "mid": v(-331.3, 2.93) * mm, "end": v(-331.06, 2.73) * mm});
            skArc(sketch, "E948", {"start": v(-331.06, 2.73) * mm, "mid": v(-330.6, 2.62) * mm, "end": v(-330.13, 2.63) * mm});
            skArc(sketch, "E949", {"start": v(-330.13, 2.63) * mm, "mid": v(-328.48, 2.86) * mm, "end": v(-326.82, 3.12) * mm});
            skArc(sketch, "E950", {"start": v(-326.82, 3.12) * mm, "mid": v(-323.34, 3.86) * mm, "end": v(-319.95, 4.96) * mm});
            skArc(sketch, "E951", {"start": v(-319.95, 4.96) * mm, "mid": v(-316.93, 6.36) * mm, "end": v(-314.1, 8.14) * mm});
            skArc(sketch, "E952", {"start": v(-314.1, 8.14) * mm, "mid": v(-311.8, 10.07) * mm, "end": v(-309.81, 12.32) * mm});
            skArc(sketch, "E953", {"start": v(-309.81, 12.32) * mm, "mid": v(-308.41, 14.6) * mm, "end": v(-307.5, 17.1) * mm});
            skArc(sketch, "E954", {"start": v(-307.5, 17.1) * mm, "mid": v(-307.42, 18.81) * mm, "end": v(-308, 20.42) * mm});
            skArc(sketch, "E955", {"start": v(-308, 20.42) * mm, "mid": v(-309.17, 21.75) * mm, "end": v(-310.73, 22.6) * mm});
            skArc(sketch, "E956", {"start": v(-310.73, 22.6) * mm, "mid": v(-312.87, 23) * mm, "end": v(-315.04, 22.85) * mm});
            skArc(sketch, "E957", {"start": v(-315.04, 22.85) * mm, "mid": v(-317.34, 22.15) * mm, "end": v(-319.47, 21.03) * mm});
            skArc(sketch, "E958", {"start": v(-171.1, 20.72) * mm, "mid": v(-172.55, 19.6) * mm, "end": v(-173.82, 18.28) * mm});
            skArc(sketch, "E959", {"start": v(-173.82, 18.28) * mm, "mid": v(-175.47, 16.2) * mm, "end": v(-177.02, 14.06) * mm});
            skArc(sketch, "E960", {"start": v(-177.02, 14.06) * mm, "mid": v(-178.53, 11.72) * mm, "end": v(-179.93, 9.32) * mm});
            skArc(sketch, "E961", {"start": v(-179.93, 9.32) * mm, "mid": v(-180.97, 7.23) * mm, "end": v(-181.83, 5.07) * mm});
            skLineSegment(sketch, "E962", {"start": v(-181.83, 5.07) * mm, "end": v(-182.78, 2.33) * mm});
            skLineSegment(sketch, "E963", {"start": v(-182.78, 2.33) * mm, "end": v(-178.14, 3.08) * mm});
            skArc(sketch, "E964", {"start": v(-178.14, 3.08) * mm, "mid": v(-176.1, 3.45) * mm, "end": v(-174.07, 3.9) * mm});
            skArc(sketch, "E965", {"start": v(-174.07, 3.9) * mm, "mid": v(-172.4, 4.37) * mm, "end": v(-170.75, 4.94) * mm});
            skArc(sketch, "E966", {"start": v(-170.75, 4.94) * mm, "mid": v(-169.25, 5.6) * mm, "end": v(-167.8, 6.34) * mm});
            skArc(sketch, "E967", {"start": v(-167.8, 6.34) * mm, "mid": v(-166.32, 7.24) * mm, "end": v(-164.89, 8.23) * mm});
            skArc(sketch, "E968", {"start": v(-164.89, 8.23) * mm, "mid": v(-163.14, 9.72) * mm, "end": v(-161.63, 11.45) * mm});
            skArc(sketch, "E969", {"start": v(-161.63, 11.45) * mm, "mid": v(-160.43, 13.33) * mm, "end": v(-159.53, 15.37) * mm});
            skArc(sketch, "E970", {"start": v(-159.53, 15.37) * mm, "mid": v(-159.09, 17.2) * mm, "end": v(-159, 19.1) * mm});
            skArc(sketch, "E971", {"start": v(-159, 19.1) * mm, "mid": v(-159.35, 20.56) * mm, "end": v(-160.2, 21.8) * mm});
            skArc(sketch, "E972", {"start": v(-160.2, 21.8) * mm, "mid": v(-161.08, 22.45) * mm, "end": v(-162.12, 22.8) * mm});
            skArc(sketch, "E973", {"start": v(-162.12, 22.8) * mm, "mid": v(-163.55, 22.95) * mm, "end": v(-164.99, 22.9) * mm});
            skArc(sketch, "E974", {"start": v(-164.99, 22.9) * mm, "mid": v(-166.61, 22.64) * mm, "end": v(-168.2, 22.19) * mm});
            skArc(sketch, "E975", {"start": v(-168.2, 22.19) * mm, "mid": v(-169.7, 21.54) * mm, "end": v(-171.1, 20.72) * mm});
            skPoint(sketch, "E976", {"position": v(-189.6, 240.81) * mm});
            skPoint(sketch, "E977", {"position": v(389.57, -267.64) * mm});
            skPoint(sketch, "E978", {"position": v(476.14, -273.73) * mm});
            skSolve(sketch);
        }
        {
            var Q0;
            Q0=makeQuery(id+"F0.imprint","IMPRINT",FACE,{"disambiguationData":[TD([[makeQuery(id+"F0.imprint","IMPRINT",EDGE,{"derivedFrom":sQuery(id+"F0.wireOp",EDGE,"E144")}),-1.0]])]});
            var Q1;
            Q1=makeQuery(id+"F0.imprint","IMPRINT",FACE,{"disambiguationData":[TD([[makeQuery(id+"F0.imprint","IMPRINT",EDGE,{"derivedFrom":sQuery(id+"F0.wireOp",EDGE,"E476")}),-1.0]])]});
            var Q2;
            Q2=makeQuery(id+"F0.imprint","IMPRINT",FACE,{"disambiguationData":[TD([[makeQuery(id+"F0.imprint","IMPRINT",EDGE,{"derivedFrom":sQuery(id+"F0.wireOp",EDGE,"E330")}),-1.0]])]});
            var Q3;
            Q3=makeQuery(id+"F0.imprint","IMPRINT",FACE,{"disambiguationData":[TD([[makeQuery(id+"F0.imprint","IMPRINT",EDGE,{"derivedFrom":sQuery(id+"F0.wireOp",EDGE,"E526")}),-1.0]])]});
            var Q4;
            Q4=makeQuery(id+"F0.imprint","IMPRINT",FACE,{"disambiguationData":[TD([[makeQuery(id+"F0.imprint","IMPRINT",EDGE,{"derivedFrom":sQuery(id+"F0.wireOp",EDGE,"E570")}),-1.0]])]});
            var Q5;
            Q5=makeQuery(id+"F0.imprint","IMPRINT",FACE,{"disambiguationData":[TD([[makeQuery(id+"F0.imprint","IMPRINT",EDGE,{"derivedFrom":sQuery(id+"F0.wireOp",EDGE,"E628")}),-1.0]])]});
            var Q6;
            Q6=makeQuery(id+"F0.imprint","IMPRINT",FACE,{"disambiguationData":[TD([[makeQuery(id+"F0.imprint","IMPRINT",EDGE,{"derivedFrom":sQuery(id+"F0.wireOp",EDGE,"E190")}),-1.0]])]});
            var Q7;
            Q7=makeQuery(id+"F0.imprint","IMPRINT",FACE,{"disambiguationData":[TD([[makeQuery(id+"F0.imprint","IMPRINT",EDGE,{"derivedFrom":sQuery(id+"F0.wireOp",EDGE,"E440")}),-1.0]])]});
            var Q8;
            Q8=makeQuery(id+"F0.imprint","IMPRINT",FACE,{"disambiguationData":[TD([[makeQuery(id+"F0.imprint","IMPRINT",EDGE,{"derivedFrom":sQuery(id+"F0.wireOp",EDGE,"E758")}),-1.0]])]});
            var Q9;
            Q9=makeQuery(id+"F0.imprint","IMPRINT",FACE,{"disambiguationData":[TD([[makeQuery(id+"F0.imprint","IMPRINT",EDGE,{"derivedFrom":sQuery(id+"F0.wireOp",EDGE,"E834")}),-1.0]])]});
            var Q10;
            Q10=makeQuery(id+"F0.imprint","IMPRINT",FACE,{"disambiguationData":[TD([[makeQuery(id+"F0.imprint","IMPRINT",EDGE,{"derivedFrom":sQuery(id+"F0.wireOp",EDGE,"E292")}),-1.0]])]});
            var Q11;
            Q11=makeQuery(id+"F0.imprint","IMPRINT",FACE,{"disambiguationData":[TD([[makeQuery(id+"F0.imprint","IMPRINT",EDGE,{"derivedFrom":sQuery(id+"F0.wireOp",EDGE,"E682")}),-1.0]])]});
            var Q12;
            Q12=makeQuery(id+"F0.imprint","IMPRINT",FACE,{"disambiguationData":[TD([[makeQuery(id+"F0.imprint","IMPRINT",EDGE,{"derivedFrom":sQuery(id+"F0.wireOp",EDGE,"E714")}),-1.0]])]});
            var Q13;
            Q13=makeQuery(id+"F0.imprint","IMPRINT",FACE,{"disambiguationData":[TD([[makeQuery(id+"F0.imprint","IMPRINT",EDGE,{"derivedFrom":sQuery(id+"F0.wireOp",EDGE,"E8")}),-1.0]])]});
            var Q14;
            Q14=makeQuery(id+"F0.imprint","IMPRINT",FACE,{"disambiguationData":[TD([[makeQuery(id+"F0.imprint","IMPRINT",EDGE,{"derivedFrom":sQuery(id+"F0.wireOp",EDGE,"E124")}),-1.0]])]});
            extrude(context, id + "F1", {"entities" : qUnion([Q0, Q1, Q2, Q3, Q4, Q5, Q6, Q7, Q8, Q9, Q10, Q11, Q12, Q13, Q14]), "depth" : 50 * mm, "offsetDistance" : 25 * mm});
        }
    });
